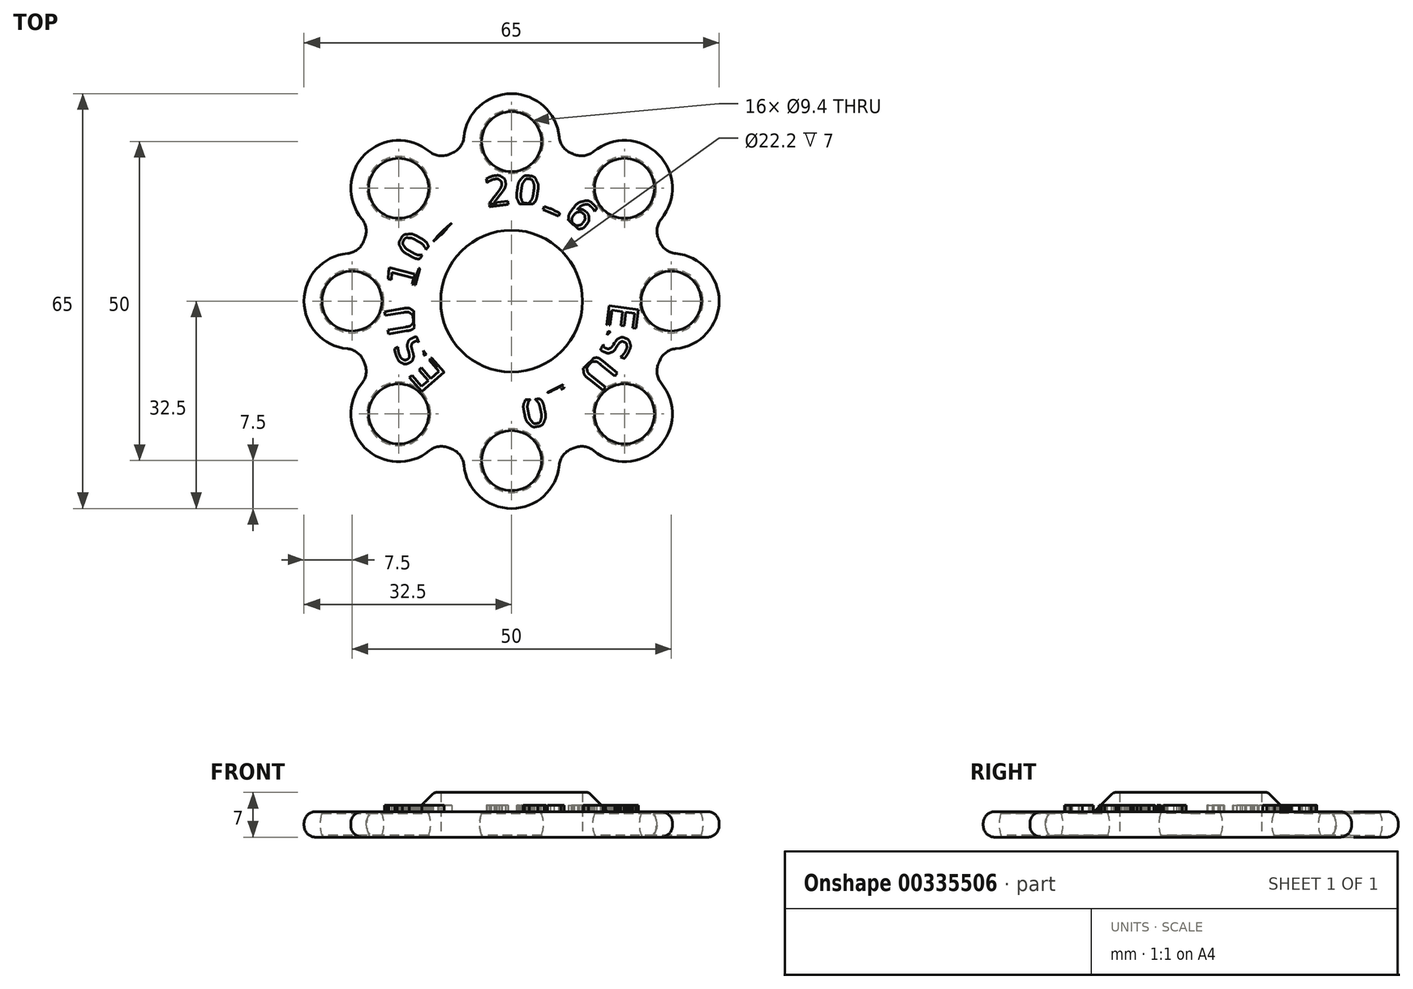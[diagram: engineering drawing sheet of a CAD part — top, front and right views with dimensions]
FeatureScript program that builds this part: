
annotation { "Feature Type Name" : "Feature", "Feature Type Description" : "" }
export const myFeature = defineFeature(function(context is Context, id is Id, definition is map)
    precondition{}
    {
        {
            var Q0;
            Q0=qCreatedBy(makeId("Top.planeOp"),FACE);
            var sketch = newSketch(context, id + "F0", { "sketchPlane" : qUnion([Q0])});
            skCircle(sketch, "E0", {"center": v(0, 0) * mm, "radius": 11.1 * mm});
            skPoint(sketch, "E1.0.midPoint", {"position": v(12.23, 6.82) * mm});
            skCircle(sketch, "E2", {"center": v(0, 25) * mm, "radius": 4.7 * mm});
            skCircle(sketch, "E3.1.0", {"center": v(-17.68, 17.68) * mm, "radius": 4.7 * mm});
            skCircle(sketch, "E3.2.0", {"center": v(-25, 0) * mm, "radius": 4.7 * mm});
            skCircle(sketch, "E3.3.0", {"center": v(-17.68, -17.68) * mm, "radius": 4.7 * mm});
            skCircle(sketch, "E3.4.0", {"center": v(0, -25) * mm, "radius": 4.7 * mm});
            skCircle(sketch, "E3.5.0", {"center": v(17.68, -17.68) * mm, "radius": 4.7 * mm});
            skCircle(sketch, "E3.6.0", {"center": v(25, 0) * mm, "radius": 4.7 * mm});
            skCircle(sketch, "E3.7.0", {"center": v(17.68, 17.68) * mm, "radius": 4.7 * mm});
            skCircle(sketch, "E4", {"center": v(0, 25) * mm, "radius": 7.5 * mm});
            skCircle(sketch, "E5.1.0", {"center": v(-17.68, 17.68) * mm, "radius": 7.5 * mm});
            skCircle(sketch, "E5.2.0", {"center": v(-25, 0) * mm, "radius": 7.5 * mm});
            skCircle(sketch, "E5.3.0", {"center": v(-17.68, -17.68) * mm, "radius": 7.5 * mm});
            skCircle(sketch, "E5.4.0", {"center": v(0, -25) * mm, "radius": 7.5 * mm});
            skCircle(sketch, "E5.5.0", {"center": v(17.68, -17.68) * mm, "radius": 7.5 * mm});
            skCircle(sketch, "E5.6.0", {"center": v(25, 0) * mm, "radius": 7.5 * mm});
            skCircle(sketch, "E5.7.0", {"center": v(17.68, 17.68) * mm, "radius": 7.5 * mm});
            skCircle(sketch, "E6", {"center": v(0, 0) * mm, "radius": 25 * mm});
            skSolve(sketch);
        }
        {
            var Q0;
            Q0=makeQuery(id+"F0.imprint","IMPRINT",FACE,{"disambiguationData":[TD([[makeQuery(id+"F0.imprint","IMPRINT",EDGE,{"derivedFrom":sQuery(id+"F0.wireOp",EDGE,"E0")}),-1.0]])]});
            var Q1;
            {var subQ0=sQuery(id+"F0.wireOp",EDGE,"E6");var subQ1=sQuery(id+"F0.wireOp",EDGE,"E3.3.0");var subQ2=makeQuery(id+"F0.imprint","INTERSECT",VERTEX,{"disambiguationData":[OD(0.0)],"derivedFrom":[subQ1,subQ0]});Q1=makeQuery(id+"F0.imprint","IMPRINT",FACE,{"disambiguationData":[TD([[makeQuery(id+"F0.imprint","IMPRINT",EDGE,{"disambiguationData":[TD([[subQ2,-1.0]])],"derivedFrom":subQ1}),-1.0]])]});}
            var Q2;
            {var subQ0=sQuery(id+"F0.wireOp",EDGE,"E6");var subQ1=sQuery(id+"F0.wireOp",EDGE,"E3.3.0");var subQ2=makeQuery(id+"F0.imprint","INTERSECT",VERTEX,{"disambiguationData":[OD(0.0)],"derivedFrom":[subQ1,subQ0]});Q2=makeQuery(id+"F0.imprint","IMPRINT",FACE,{"disambiguationData":[TD([[makeQuery(id+"F0.imprint","IMPRINT",EDGE,{"disambiguationData":[TD([[subQ2,1.0]])],"derivedFrom":subQ1}),-1.0]])]});}
            var Q3;
            {var subQ0=sQuery(id+"F0.wireOp",EDGE,"E6");var subQ1=sQuery(id+"F0.wireOp",EDGE,"E3.2.0");var subQ2=makeQuery(id+"F0.imprint","INTERSECT",VERTEX,{"disambiguationData":[OD(0.0)],"derivedFrom":[subQ1,subQ0]});Q3=makeQuery(id+"F0.imprint","IMPRINT",FACE,{"disambiguationData":[TD([[makeQuery(id+"F0.imprint","IMPRINT",EDGE,{"disambiguationData":[TD([[subQ2,1.0]])],"derivedFrom":subQ1}),-1.0]])]});}
            var Q4;
            {var subQ0=sQuery(id+"F0.wireOp",EDGE,"E6");var subQ1=sQuery(id+"F0.wireOp",EDGE,"E3.2.0");var subQ2=makeQuery(id+"F0.imprint","INTERSECT",VERTEX,{"disambiguationData":[OD(0.0)],"derivedFrom":[subQ1,subQ0]});Q4=makeQuery(id+"F0.imprint","IMPRINT",FACE,{"disambiguationData":[TD([[makeQuery(id+"F0.imprint","IMPRINT",EDGE,{"disambiguationData":[TD([[subQ2,-1.0]])],"derivedFrom":subQ1}),-1.0]])]});}
            var Q5;
            {var subQ0=sQuery(id+"F0.wireOp",EDGE,"E6");var subQ1=sQuery(id+"F0.wireOp",EDGE,"E3.1.0");var subQ2=makeQuery(id+"F0.imprint","INTERSECT",VERTEX,{"disambiguationData":[OD(0.0)],"derivedFrom":[subQ1,subQ0]});Q5=makeQuery(id+"F0.imprint","IMPRINT",FACE,{"disambiguationData":[TD([[makeQuery(id+"F0.imprint","IMPRINT",EDGE,{"disambiguationData":[TD([[subQ2,-1.0]])],"derivedFrom":subQ1}),-1.0]])]});}
            var Q6;
            {var subQ0=sQuery(id+"F0.wireOp",EDGE,"E6");var subQ1=sQuery(id+"F0.wireOp",EDGE,"E3.1.0");var subQ2=makeQuery(id+"F0.imprint","INTERSECT",VERTEX,{"disambiguationData":[OD(0.0)],"derivedFrom":[subQ1,subQ0]});Q6=makeQuery(id+"F0.imprint","IMPRINT",FACE,{"disambiguationData":[TD([[makeQuery(id+"F0.imprint","IMPRINT",EDGE,{"disambiguationData":[TD([[subQ2,1.0]])],"derivedFrom":subQ1}),-1.0]])]});}
            var Q7;
            {var subQ0=sQuery(id+"F0.wireOp",EDGE,"E6");var subQ1=sQuery(id+"F0.wireOp",EDGE,"E2");var subQ2=makeQuery(id+"F0.imprint","INTERSECT",VERTEX,{"disambiguationData":[OD(0.0)],"derivedFrom":[subQ1,subQ0]});Q7=makeQuery(id+"F0.imprint","IMPRINT",FACE,{"disambiguationData":[TD([[makeQuery(id+"F0.imprint","IMPRINT",EDGE,{"disambiguationData":[TD([[subQ2,1.0]])],"derivedFrom":subQ1}),-1.0]])]});}
            var Q8;
            {var subQ0=sQuery(id+"F0.wireOp",EDGE,"E6");var subQ1=sQuery(id+"F0.wireOp",EDGE,"E2");var subQ2=makeQuery(id+"F0.imprint","INTERSECT",VERTEX,{"disambiguationData":[OD(0.0)],"derivedFrom":[subQ1,subQ0]});Q8=makeQuery(id+"F0.imprint","IMPRINT",FACE,{"disambiguationData":[TD([[makeQuery(id+"F0.imprint","IMPRINT",EDGE,{"disambiguationData":[TD([[subQ2,-1.0]])],"derivedFrom":subQ1}),-1.0]])]});}
            var Q9;
            {var subQ0=sQuery(id+"F0.wireOp",EDGE,"E6");var subQ1=sQuery(id+"F0.wireOp",EDGE,"E3.7.0");var subQ2=makeQuery(id+"F0.imprint","INTERSECT",VERTEX,{"disambiguationData":[OD(0.0)],"derivedFrom":[subQ1,subQ0]});Q9=makeQuery(id+"F0.imprint","IMPRINT",FACE,{"disambiguationData":[TD([[makeQuery(id+"F0.imprint","IMPRINT",EDGE,{"disambiguationData":[TD([[subQ2,1.0]])],"derivedFrom":subQ1}),-1.0]])]});}
            var Q10;
            {var subQ0=sQuery(id+"F0.wireOp",EDGE,"E6");var subQ1=sQuery(id+"F0.wireOp",EDGE,"E3.7.0");var subQ2=makeQuery(id+"F0.imprint","INTERSECT",VERTEX,{"disambiguationData":[OD(0.0)],"derivedFrom":[subQ1,subQ0]});Q10=makeQuery(id+"F0.imprint","IMPRINT",FACE,{"disambiguationData":[TD([[makeQuery(id+"F0.imprint","IMPRINT",EDGE,{"disambiguationData":[TD([[subQ2,-1.0]])],"derivedFrom":subQ1}),-1.0]])]});}
            var Q11;
            {var subQ0=sQuery(id+"F0.wireOp",EDGE,"E6");var subQ1=sQuery(id+"F0.wireOp",EDGE,"E3.6.0");var subQ2=makeQuery(id+"F0.imprint","INTERSECT",VERTEX,{"disambiguationData":[OD(0.0)],"derivedFrom":[subQ1,subQ0]});Q11=makeQuery(id+"F0.imprint","IMPRINT",FACE,{"disambiguationData":[TD([[makeQuery(id+"F0.imprint","IMPRINT",EDGE,{"disambiguationData":[TD([[subQ2,-1.0]])],"derivedFrom":subQ1}),-1.0]])]});}
            var Q12;
            {var subQ0=sQuery(id+"F0.wireOp",EDGE,"E6");var subQ1=sQuery(id+"F0.wireOp",EDGE,"E3.6.0");var subQ2=makeQuery(id+"F0.imprint","INTERSECT",VERTEX,{"disambiguationData":[OD(0.0)],"derivedFrom":[subQ1,subQ0]});Q12=makeQuery(id+"F0.imprint","IMPRINT",FACE,{"disambiguationData":[TD([[makeQuery(id+"F0.imprint","IMPRINT",EDGE,{"disambiguationData":[TD([[subQ2,1.0]])],"derivedFrom":subQ1}),-1.0]])]});}
            var Q13;
            {var subQ0=sQuery(id+"F0.wireOp",EDGE,"E6");var subQ1=sQuery(id+"F0.wireOp",EDGE,"E3.5.0");var subQ2=makeQuery(id+"F0.imprint","INTERSECT",VERTEX,{"disambiguationData":[OD(0.0)],"derivedFrom":[subQ1,subQ0]});Q13=makeQuery(id+"F0.imprint","IMPRINT",FACE,{"disambiguationData":[TD([[makeQuery(id+"F0.imprint","IMPRINT",EDGE,{"disambiguationData":[TD([[subQ2,1.0]])],"derivedFrom":subQ1}),-1.0]])]});}
            var Q14;
            {var subQ0=sQuery(id+"F0.wireOp",EDGE,"E6");var subQ1=sQuery(id+"F0.wireOp",EDGE,"E3.5.0");var subQ2=makeQuery(id+"F0.imprint","INTERSECT",VERTEX,{"disambiguationData":[OD(0.0)],"derivedFrom":[subQ1,subQ0]});Q14=makeQuery(id+"F0.imprint","IMPRINT",FACE,{"disambiguationData":[TD([[makeQuery(id+"F0.imprint","IMPRINT",EDGE,{"disambiguationData":[TD([[subQ2,-1.0]])],"derivedFrom":subQ1}),-1.0]])]});}
            var Q15;
            {var subQ0=sQuery(id+"F0.wireOp",EDGE,"E6");var subQ1=sQuery(id+"F0.wireOp",EDGE,"E3.4.0");var subQ2=makeQuery(id+"F0.imprint","INTERSECT",VERTEX,{"disambiguationData":[OD(0.0)],"derivedFrom":[subQ1,subQ0]});Q15=makeQuery(id+"F0.imprint","IMPRINT",FACE,{"disambiguationData":[TD([[makeQuery(id+"F0.imprint","IMPRINT",EDGE,{"disambiguationData":[TD([[subQ2,1.0]])],"derivedFrom":subQ1}),-1.0]])]});}
            var Q16;
            {var subQ0=sQuery(id+"F0.wireOp",EDGE,"E6");var subQ1=sQuery(id+"F0.wireOp",EDGE,"E3.4.0");var subQ2=makeQuery(id+"F0.imprint","INTERSECT",VERTEX,{"disambiguationData":[OD(0.0)],"derivedFrom":[subQ1,subQ0]});Q16=makeQuery(id+"F0.imprint","IMPRINT",FACE,{"disambiguationData":[TD([[makeQuery(id+"F0.imprint","IMPRINT",EDGE,{"disambiguationData":[TD([[subQ2,-1.0]])],"derivedFrom":subQ1}),-1.0]])]});}
            extrude(context, id + "F1", {"entities" : qUnion([Q0, Q1, Q2, Q3, Q4, Q5, Q6, Q7, Q8, Q9, Q10, Q11, Q12, Q13, Q14, Q15, Q16]), "depth" : 2 * mm, "hasSecondDirection" : true, "secondDirectionOppositeDirection" : true, "secondDirectionDepth" : 2 * mm});
        }
        {
            var Q0;
            {var subQ0=sQuery(id+"F0.wireOp",EDGE,"E6");var subQ1=sQuery(id+"F0.wireOp",EDGE,"E5.4.0");Q0=makeQuery(id+"F1.opExtrude","SWEPT_EDGE",EDGE,{"disambiguationData":[OSD([subQ1,subQ0]),TDD([makeQuery(id+"F0.imprint","INTERSECT",VERTEX,{"disambiguationData":[OD(0.0)],"derivedFrom":[subQ1,subQ0]})])]});}
            var Q1;
            {var subQ0=sQuery(id+"F0.wireOp",EDGE,"E6");var subQ1=sQuery(id+"F0.wireOp",EDGE,"E5.2.0");Q1=makeQuery(id+"F1.opExtrude","SWEPT_EDGE",EDGE,{"disambiguationData":[OSD([subQ1,subQ0]),TDD([makeQuery(id+"F0.imprint","INTERSECT",VERTEX,{"disambiguationData":[OD(1.0)],"derivedFrom":[subQ1,subQ0]})])]});}
            var Q2;
            {var subQ0=sQuery(id+"F0.wireOp",EDGE,"E6");var subQ1=sQuery(id+"F0.wireOp",EDGE,"E5.2.0");Q2=makeQuery(id+"F1.opExtrude","SWEPT_EDGE",EDGE,{"disambiguationData":[OSD([subQ1,subQ0]),TDD([makeQuery(id+"F0.imprint","INTERSECT",VERTEX,{"disambiguationData":[OD(0.0)],"derivedFrom":[subQ1,subQ0]})])]});}
            var Q3;
            {var subQ0=sQuery(id+"F0.wireOp",EDGE,"E6");var subQ1=sQuery(id+"F0.wireOp",EDGE,"E4");Q3=makeQuery(id+"F1.opExtrude","SWEPT_EDGE",EDGE,{"disambiguationData":[OSD([subQ1,subQ0]),TDD([makeQuery(id+"F0.imprint","INTERSECT",VERTEX,{"disambiguationData":[OD(1.0)],"derivedFrom":[subQ1,subQ0]})])]});}
            var Q4;
            {var subQ0=sQuery(id+"F0.wireOp",EDGE,"E6");var subQ1=sQuery(id+"F0.wireOp",EDGE,"E5.7.0");Q4=makeQuery(id+"F1.opExtrude","SWEPT_EDGE",EDGE,{"disambiguationData":[OSD([subQ1,subQ0]),TDD([makeQuery(id+"F0.imprint","INTERSECT",VERTEX,{"disambiguationData":[OD(1.0)],"derivedFrom":[subQ1,subQ0]})])]});}
            var Q5;
            {var subQ0=sQuery(id+"F0.wireOp",EDGE,"E6");var subQ1=sQuery(id+"F0.wireOp",EDGE,"E5.1.0");Q5=makeQuery(id+"F1.opExtrude","SWEPT_EDGE",EDGE,{"disambiguationData":[OSD([subQ1,subQ0]),TDD([makeQuery(id+"F0.imprint","INTERSECT",VERTEX,{"disambiguationData":[OD(1.0)],"derivedFrom":[subQ1,subQ0]})])]});}
            var Q6;
            {var subQ0=sQuery(id+"F0.wireOp",EDGE,"E6");var subQ1=sQuery(id+"F0.wireOp",EDGE,"E5.3.0");Q6=makeQuery(id+"F1.opExtrude","SWEPT_EDGE",EDGE,{"disambiguationData":[OSD([subQ1,subQ0]),TDD([makeQuery(id+"F0.imprint","INTERSECT",VERTEX,{"disambiguationData":[OD(0.0)],"derivedFrom":[subQ1,subQ0]})])]});}
            var Q7;
            {var subQ0=sQuery(id+"F0.wireOp",EDGE,"E6");var subQ1=sQuery(id+"F0.wireOp",EDGE,"E5.1.0");Q7=makeQuery(id+"F1.opExtrude","SWEPT_EDGE",EDGE,{"disambiguationData":[OSD([subQ1,subQ0]),TDD([makeQuery(id+"F0.imprint","INTERSECT",VERTEX,{"disambiguationData":[OD(0.0)],"derivedFrom":[subQ1,subQ0]})])]});}
            var Q8;
            {var subQ0=sQuery(id+"F0.wireOp",EDGE,"E6");var subQ1=sQuery(id+"F0.wireOp",EDGE,"E4");Q8=makeQuery(id+"F1.opExtrude","SWEPT_EDGE",EDGE,{"disambiguationData":[OSD([subQ1,subQ0]),TDD([makeQuery(id+"F0.imprint","INTERSECT",VERTEX,{"disambiguationData":[OD(0.0)],"derivedFrom":[subQ1,subQ0]})])]});}
            var Q9;
            {var subQ0=sQuery(id+"F0.wireOp",EDGE,"E6");var subQ1=sQuery(id+"F0.wireOp",EDGE,"E5.6.0");Q9=makeQuery(id+"F1.opExtrude","SWEPT_EDGE",EDGE,{"disambiguationData":[OSD([subQ1,subQ0]),TDD([makeQuery(id+"F0.imprint","INTERSECT",VERTEX,{"disambiguationData":[OD(0.0)],"derivedFrom":[subQ1,subQ0]})])]});}
            var Q10;
            {var subQ0=sQuery(id+"F0.wireOp",EDGE,"E6");var subQ1=sQuery(id+"F0.wireOp",EDGE,"E5.7.0");Q10=makeQuery(id+"F1.opExtrude","SWEPT_EDGE",EDGE,{"disambiguationData":[OSD([subQ1,subQ0]),TDD([makeQuery(id+"F0.imprint","INTERSECT",VERTEX,{"disambiguationData":[OD(0.0)],"derivedFrom":[subQ1,subQ0]})])]});}
            var Q11;
            {var subQ0=sQuery(id+"F0.wireOp",EDGE,"E6");var subQ1=sQuery(id+"F0.wireOp",EDGE,"E5.6.0");Q11=makeQuery(id+"F1.opExtrude","SWEPT_EDGE",EDGE,{"disambiguationData":[OSD([subQ1,subQ0]),TDD([makeQuery(id+"F0.imprint","INTERSECT",VERTEX,{"disambiguationData":[OD(1.0)],"derivedFrom":[subQ1,subQ0]})])]});}
            var Q12;
            {var subQ0=sQuery(id+"F0.wireOp",EDGE,"E6");var subQ1=sQuery(id+"F0.wireOp",EDGE,"E5.5.0");Q12=makeQuery(id+"F1.opExtrude","SWEPT_EDGE",EDGE,{"disambiguationData":[OSD([subQ1,subQ0]),TDD([makeQuery(id+"F0.imprint","INTERSECT",VERTEX,{"disambiguationData":[OD(1.0)],"derivedFrom":[subQ1,subQ0]})])]});}
            var Q13;
            {var subQ0=sQuery(id+"F0.wireOp",EDGE,"E6");var subQ1=sQuery(id+"F0.wireOp",EDGE,"E5.5.0");Q13=makeQuery(id+"F1.opExtrude","SWEPT_EDGE",EDGE,{"disambiguationData":[OSD([subQ1,subQ0]),TDD([makeQuery(id+"F0.imprint","INTERSECT",VERTEX,{"disambiguationData":[OD(0.0)],"derivedFrom":[subQ1,subQ0]})])]});}
            var Q14;
            {var subQ0=sQuery(id+"F0.wireOp",EDGE,"E6");var subQ1=sQuery(id+"F0.wireOp",EDGE,"E5.4.0");Q14=makeQuery(id+"F1.opExtrude","SWEPT_EDGE",EDGE,{"disambiguationData":[OSD([subQ1,subQ0]),TDD([makeQuery(id+"F0.imprint","INTERSECT",VERTEX,{"disambiguationData":[OD(1.0)],"derivedFrom":[subQ1,subQ0]})])]});}
            var Q15;
            {var subQ0=sQuery(id+"F0.wireOp",EDGE,"E6");var subQ1=sQuery(id+"F0.wireOp",EDGE,"E5.3.0");Q15=makeQuery(id+"F1.opExtrude","SWEPT_EDGE",EDGE,{"disambiguationData":[OSD([subQ1,subQ0]),TDD([makeQuery(id+"F0.imprint","INTERSECT",VERTEX,{"disambiguationData":[OD(1.0)],"derivedFrom":[subQ1,subQ0]})])]});}
            fillet(context, id + "F2", {"entities" : qUnion([Q0, Q1, Q2, Q3, Q4, Q5, Q6, Q7, Q8, Q9, Q10, Q11, Q12, Q13, Q14, Q15]), "radius" : 3 * mm, "tangentPropagation" : true, "allowEdgeOverflow" : false});
        }
        {
            var Q0;
            Q0=makeQuery(id+"F1.opExtrude","CAP_EDGE",EDGE,{"disambiguationData":[OSD([sQuery(id+"F0.wireOp",EDGE,"E5.7.0")])],"isStart":false});
            var Q1;
            Q1=makeQuery(id+"F1.opExtrude","CAP_EDGE",EDGE,{"disambiguationData":[OSD([sQuery(id+"F0.wireOp",EDGE,"E5.7.0")])],"isStart":true});
            fillet(context, id + "F3", {"entities" : qUnion([Q0, Q1]), "radius" : 1.8 * mm, "tangentPropagation" : true, "allowEdgeOverflow" : false});
        }
        {
            var Q0;
            Q0=qCreatedBy(makeId("Right.planeOp"),FACE);
            var sketch = newSketch(context, id + "F4", { "sketchPlane" : qUnion([Q0])});
            skPoint(sketch, "E7.0", {"position": v(-25, 0) * mm});
            skPoint(sketch, "E7.1", {"position": v(25, 0) * mm});
            skLineSegment(sketch, "E8", {"start": v(-25, 12.35) * mm, "end": v(-25, -14.21) * mm, "construction": true});
            skLineSegment(sketch, "E9", {"start": v(25, 12.16) * mm, "end": v(25, -14.21) * mm, "construction": true});
            skPoint(sketch, "E10", {"position": v(-25, 5) * mm});
            skPoint(sketch, "E11", {"position": v(-25, -5) * mm});
            skPoint(sketch, "E12", {"position": v(25, 5) * mm});
            skPoint(sketch, "E13", {"position": v(25, -5) * mm});
            skArc(sketch, "E14", {"start": v(-25, 5) * mm, "mid": v(-30, 0) * mm, "end": v(-25, -5) * mm});
            skArc(sketch, "E15", {"start": v(25, -5) * mm, "mid": v(30, 0) * mm, "end": v(25, 5) * mm});
            skLineSegment(sketch, "E16", {"start": v(-25, 5) * mm, "end": v(-25, -5) * mm});
            skLineSegment(sketch, "E17", {"start": v(25, 5) * mm, "end": v(25, -5) * mm});
            skLineSegment(sketch, "E18", {"start": v(0, 41.23) * mm, "end": v(0, -49.38) * mm, "construction": true});
            skSolve(sketch);
        }
        {
            var Q0;
            Q0=makeQuery(id+"F4.imprint","IMPRINT",FACE,{"disambiguationData":[TD([[makeQuery(id+"F4.imprint","IMPRINT",EDGE,{"derivedFrom":sQuery(id+"F4.wireOp",EDGE,"E14")}),1.0]])]});
            var Q1;
            Q1=sQuery(id+"F4.wireOp",EDGE,"E8");
            revolve(context, id + "F5", {"entities" : qUnion([Q0]), "axis" : qUnion([Q1]), "revolveType" : RevolveType.FULL});
        }
        {
            var Q0;
            Q0=makeQuery(id+"F4.imprint","IMPRINT",FACE,{"disambiguationData":[TD([[makeQuery(id+"F4.imprint","IMPRINT",EDGE,{"derivedFrom":sQuery(id+"F4.wireOp",EDGE,"E15")}),1.0]])]});
            var Q1;
            Q1=sQuery(id+"F4.wireOp",EDGE,"E9");
            revolve(context, id + "F6", {"entities" : qUnion([Q0]), "axis" : qUnion([Q1]), "revolveType" : RevolveType.FULL});
        }
        {
            var Q0;
            Q0=makeQuery(id+"F6.opRevolve","SWEPT_BODY",BODY,{"disambiguationData":[OSD([sQuery(id+"F4.wireOp",EDGE,"E15"),sQuery(id+"F4.wireOp",EDGE,"E17")])]});
            var Q1;
            Q1=makeQuery(id+"F5.opRevolve","SWEPT_BODY",BODY,{"disambiguationData":[OSD([sQuery(id+"F4.wireOp",EDGE,"E14"),sQuery(id+"F4.wireOp",EDGE,"E16")])]});
            var Q2;
            Q2=makeQuery(id+"F1.opExtrude","SWEPT_BODY",BODY,{"disambiguationData":[OSD([sQuery(id+"F0.wireOp",EDGE,"E0"),sQuery(id+"F0.wireOp",EDGE,"E2"),sQuery(id+"F0.wireOp",EDGE,"E3.1.0"),sQuery(id+"F0.wireOp",EDGE,"E3.2.0"),sQuery(id+"F0.wireOp",EDGE,"E3.3.0"),sQuery(id+"F0.wireOp",EDGE,"E3.4.0"),sQuery(id+"F0.wireOp",EDGE,"E3.5.0"),sQuery(id+"F0.wireOp",EDGE,"E3.6.0"),sQuery(id+"F0.wireOp",EDGE,"E3.7.0"),sQuery(id+"F0.wireOp",EDGE,"E4"),sQuery(id+"F0.wireOp",EDGE,"E5.1.0"),sQuery(id+"F0.wireOp",EDGE,"E5.2.0"),sQuery(id+"F0.wireOp",EDGE,"E5.3.0"),sQuery(id+"F0.wireOp",EDGE,"E5.4.0"),sQuery(id+"F0.wireOp",EDGE,"E5.5.0"),sQuery(id+"F0.wireOp",EDGE,"E5.6.0"),sQuery(id+"F0.wireOp",EDGE,"E5.7.0"),sQuery(id+"F0.wireOp",EDGE,"E6")])]});
            booleanBodies(context, id + "F7", {"operationType" : BooleanOperationType.SUBTRACTION, "tools" : qUnion([Q0, Q1]), "targets" : qUnion([Q2])});
        }
        {
            var Q0;
            Q0=qCreatedBy(makeId("Front.planeOp"),FACE);
            var sketch = newSketch(context, id + "F8", { "sketchPlane" : qUnion([Q0])});
            skPoint(sketch, "E19.0", {"position": v(-25, 0) * mm});
            skPoint(sketch, "E19.1", {"position": v(25, 0) * mm});
            skLineSegment(sketch, "E20", {"start": v(-25, 18.9) * mm, "end": v(-25, -20.91) * mm, "construction": true});
            skLineSegment(sketch, "E21", {"start": v(25, 20.02) * mm, "end": v(25, -22.02) * mm, "construction": true});
            skPoint(sketch, "E22", {"position": v(-25, 5) * mm});
            skPoint(sketch, "E23", {"position": v(-25, -5) * mm});
            skPoint(sketch, "E24", {"position": v(25, 5) * mm});
            skPoint(sketch, "E25", {"position": v(25, -5) * mm});
            skArc(sketch, "E26", {"start": v(-25, 5) * mm, "mid": v(-30, 0) * mm, "end": v(-25, -5) * mm});
            skArc(sketch, "E27", {"start": v(25, -5) * mm, "mid": v(30, 0) * mm, "end": v(25, 5) * mm});
            skLineSegment(sketch, "E28", {"start": v(-25, 5) * mm, "end": v(-25, -5) * mm});
            skLineSegment(sketch, "E29", {"start": v(25, 5) * mm, "end": v(25, -5) * mm});
            skSolve(sketch);
        }
        {
            var Q0;
            Q0=makeQuery(id+"F8.imprint","IMPRINT",FACE,{"disambiguationData":[TD([[makeQuery(id+"F8.imprint","IMPRINT",EDGE,{"derivedFrom":sQuery(id+"F8.wireOp",EDGE,"E26")}),1.0]])]});
            var Q1;
            Q1=sQuery(id+"F8.wireOp",EDGE,"E20");
            revolve(context, id + "F9", {"entities" : qUnion([Q0]), "axis" : qUnion([Q1]), "revolveType" : RevolveType.FULL});
        }
        {
            var Q0;
            Q0=makeQuery(id+"F8.imprint","IMPRINT",FACE,{"disambiguationData":[TD([[makeQuery(id+"F8.imprint","IMPRINT",EDGE,{"derivedFrom":sQuery(id+"F8.wireOp",EDGE,"E27")}),1.0]])]});
            var Q1;
            Q1=sQuery(id+"F8.wireOp",EDGE,"E21");
            revolve(context, id + "F10", {"entities" : qUnion([Q0]), "axis" : qUnion([Q1]), "revolveType" : RevolveType.FULL});
        }
        {
            var Q0;
            Q0=makeQuery(id+"F9.opRevolve","SWEPT_BODY",BODY,{"disambiguationData":[OSD([sQuery(id+"F8.wireOp",EDGE,"E26"),sQuery(id+"F8.wireOp",EDGE,"E28")])]});
            var Q1;
            Q1=makeQuery(id+"F10.opRevolve","SWEPT_BODY",BODY,{"disambiguationData":[OSD([sQuery(id+"F8.wireOp",EDGE,"E27"),sQuery(id+"F8.wireOp",EDGE,"E29")])]});
            var Q2;
            Q2=makeQuery(id+"F1.opExtrude","SWEPT_BODY",BODY,{"disambiguationData":[OSD([sQuery(id+"F0.wireOp",EDGE,"E0"),sQuery(id+"F0.wireOp",EDGE,"E2"),sQuery(id+"F0.wireOp",EDGE,"E3.1.0"),sQuery(id+"F0.wireOp",EDGE,"E3.2.0"),sQuery(id+"F0.wireOp",EDGE,"E3.3.0"),sQuery(id+"F0.wireOp",EDGE,"E3.4.0"),sQuery(id+"F0.wireOp",EDGE,"E3.5.0"),sQuery(id+"F0.wireOp",EDGE,"E3.6.0"),sQuery(id+"F0.wireOp",EDGE,"E3.7.0"),sQuery(id+"F0.wireOp",EDGE,"E4"),sQuery(id+"F0.wireOp",EDGE,"E5.1.0"),sQuery(id+"F0.wireOp",EDGE,"E5.2.0"),sQuery(id+"F0.wireOp",EDGE,"E5.3.0"),sQuery(id+"F0.wireOp",EDGE,"E5.4.0"),sQuery(id+"F0.wireOp",EDGE,"E5.5.0"),sQuery(id+"F0.wireOp",EDGE,"E5.6.0"),sQuery(id+"F0.wireOp",EDGE,"E5.7.0"),sQuery(id+"F0.wireOp",EDGE,"E6")])]});
            booleanBodies(context, id + "F11", {"operationType" : BooleanOperationType.SUBTRACTION, "tools" : qUnion([Q0, Q1]), "targets" : qUnion([Q2])});
        }
        {
            var Q0;
            Q0=qCreatedBy(makeId("Front.planeOp"),FACE);
            var Q1;
            Q1=sQuery(id+"F0.wireOp",VERTEX,"E3.3.0.center");
            cPlane(context, id + "F12", {"entities" : qUnion([Q0, Q1]), "cplaneType" : CPlaneType.PLANE_POINT, "offset" : 25 * mm, "width" : 150 * mm, "height" : 150 * mm});
        }
        {
            var Q0;
            Q0=qCreatedBy(id+"F12.planeOp",FACE);
            var sketch = newSketch(context, id + "F13", { "sketchPlane" : qUnion([Q0])});
            skPoint(sketch, "E30.0", {"position": v(-17.68, 0) * mm});
            skPoint(sketch, "E30.1", {"position": v(17.68, 0) * mm});
            skLineSegment(sketch, "E31", {"start": v(-17.68, 20.76) * mm, "end": v(-17.68, -25.8) * mm, "construction": true});
            skLineSegment(sketch, "E32", {"start": v(17.68, 18.25) * mm, "end": v(17.68, -22.97) * mm, "construction": true});
            skPoint(sketch, "E33", {"position": v(-17.68, 5) * mm});
            skPoint(sketch, "E34", {"position": v(-17.68, -5) * mm});
            skPoint(sketch, "E35", {"position": v(17.68, -5) * mm});
            skPoint(sketch, "E36", {"position": v(17.68, 5) * mm});
            skArc(sketch, "E37", {"start": v(-17.68, 5) * mm, "mid": v(-22.68, 0) * mm, "end": v(-17.68, -5) * mm});
            skArc(sketch, "E38", {"start": v(17.68, -5) * mm, "mid": v(22.68, 0) * mm, "end": v(17.68, 5) * mm});
            skLineSegment(sketch, "E39", {"start": v(-17.68, 5) * mm, "end": v(-17.68, -5) * mm});
            skLineSegment(sketch, "E40", {"start": v(17.68, 5) * mm, "end": v(17.68, -5) * mm});
            skSolve(sketch);
        }
        {
            var Q0;
            Q0=makeQuery(id+"F13.imprint","IMPRINT",FACE,{"disambiguationData":[TD([[makeQuery(id+"F13.imprint","IMPRINT",EDGE,{"derivedFrom":sQuery(id+"F13.wireOp",EDGE,"E37")}),1.0]])]});
            var Q1;
            Q1=sQuery(id+"F13.wireOp",EDGE,"E31");
            revolve(context, id + "F14", {"entities" : qUnion([Q0]), "axis" : qUnion([Q1]), "revolveType" : RevolveType.FULL});
        }
        {
            var Q0;
            Q0=makeQuery(id+"F13.imprint","IMPRINT",FACE,{"disambiguationData":[TD([[makeQuery(id+"F13.imprint","IMPRINT",EDGE,{"derivedFrom":sQuery(id+"F13.wireOp",EDGE,"E38")}),1.0]])]});
            var Q1;
            Q1=sQuery(id+"F13.wireOp",EDGE,"E32");
            revolve(context, id + "F15", {"entities" : qUnion([Q0]), "axis" : qUnion([Q1]), "revolveType" : RevolveType.FULL});
        }
        {
            var Q0;
            Q0=makeQuery(id+"F15.opRevolve","SWEPT_BODY",BODY,{"disambiguationData":[OSD([sQuery(id+"F13.wireOp",EDGE,"E38"),sQuery(id+"F13.wireOp",EDGE,"E40")])]});
            var Q1;
            Q1=makeQuery(id+"F14.opRevolve","SWEPT_BODY",BODY,{"disambiguationData":[OSD([sQuery(id+"F13.wireOp",EDGE,"E37"),sQuery(id+"F13.wireOp",EDGE,"E39")])]});
            var Q2;
            Q2=makeQuery(id+"F1.opExtrude","SWEPT_BODY",BODY,{"disambiguationData":[OSD([sQuery(id+"F0.wireOp",EDGE,"E0"),sQuery(id+"F0.wireOp",EDGE,"E2"),sQuery(id+"F0.wireOp",EDGE,"E3.1.0"),sQuery(id+"F0.wireOp",EDGE,"E3.2.0"),sQuery(id+"F0.wireOp",EDGE,"E3.3.0"),sQuery(id+"F0.wireOp",EDGE,"E3.4.0"),sQuery(id+"F0.wireOp",EDGE,"E3.5.0"),sQuery(id+"F0.wireOp",EDGE,"E3.6.0"),sQuery(id+"F0.wireOp",EDGE,"E3.7.0"),sQuery(id+"F0.wireOp",EDGE,"E4"),sQuery(id+"F0.wireOp",EDGE,"E5.1.0"),sQuery(id+"F0.wireOp",EDGE,"E5.2.0"),sQuery(id+"F0.wireOp",EDGE,"E5.3.0"),sQuery(id+"F0.wireOp",EDGE,"E5.4.0"),sQuery(id+"F0.wireOp",EDGE,"E5.5.0"),sQuery(id+"F0.wireOp",EDGE,"E5.6.0"),sQuery(id+"F0.wireOp",EDGE,"E5.7.0"),sQuery(id+"F0.wireOp",EDGE,"E6")])]});
            booleanBodies(context, id + "F16", {"operationType" : BooleanOperationType.SUBTRACTION, "tools" : qUnion([Q0, Q1]), "targets" : qUnion([Q2])});
        }
        {
            var Q0;
            Q0=qCreatedBy(makeId("Front.planeOp"),FACE);
            var Q1;
            Q1=sQuery(id+"F0.wireOp",VERTEX,"E5.7.0.center");
            cPlane(context, id + "F17", {"entities" : qUnion([Q0, Q1]), "cplaneType" : CPlaneType.PLANE_POINT, "offset" : 25 * mm, "width" : 150 * mm, "height" : 150 * mm});
        }
        {
            var Q0;
            Q0=qCreatedBy(id+"F17.planeOp",FACE);
            var sketch = newSketch(context, id + "F18", { "sketchPlane" : qUnion([Q0])});
            skPoint(sketch, "E41.0", {"position": v(17.68, 0) * mm});
            skPoint(sketch, "E41.1", {"position": v(-17.68, 0) * mm});
            skLineSegment(sketch, "E42", {"start": v(17.68, 20.69) * mm, "end": v(17.68, -19.13) * mm, "construction": true});
            skLineSegment(sketch, "E43", {"start": v(-17.68, 22.25) * mm, "end": v(-17.68, -19.13) * mm, "construction": true});
            skPoint(sketch, "E44", {"position": v(17.68, 5) * mm});
            skPoint(sketch, "E45", {"position": v(-17.68, 5) * mm});
            skPoint(sketch, "E46", {"position": v(17.68, -5) * mm});
            skPoint(sketch, "E47", {"position": v(-17.68, -5) * mm});
            skArc(sketch, "E48", {"start": v(17.68, -5) * mm, "mid": v(22.68, 0) * mm, "end": v(17.68, 5) * mm});
            skArc(sketch, "E49", {"start": v(-17.68, 5) * mm, "mid": v(-22.68, 0) * mm, "end": v(-17.68, -5) * mm});
            skLineSegment(sketch, "E50", {"start": v(17.68, 5) * mm, "end": v(17.68, -5) * mm});
            skLineSegment(sketch, "E51", {"start": v(-17.68, 5) * mm, "end": v(-17.68, -5) * mm});
            skSolve(sketch);
        }
        {
            var Q0;
            Q0=makeQuery(id+"F18.imprint","IMPRINT",FACE,{"disambiguationData":[TD([[makeQuery(id+"F18.imprint","IMPRINT",EDGE,{"derivedFrom":sQuery(id+"F18.wireOp",EDGE,"E48")}),1.0]])]});
            var Q1;
            Q1=sQuery(id+"F18.wireOp",EDGE,"E42");
            revolve(context, id + "F19", {"entities" : qUnion([Q0]), "axis" : qUnion([Q1]), "revolveType" : RevolveType.FULL});
        }
        {
            var Q0;
            Q0=makeQuery(id+"F18.imprint","IMPRINT",FACE,{"disambiguationData":[TD([[makeQuery(id+"F18.imprint","IMPRINT",EDGE,{"derivedFrom":sQuery(id+"F18.wireOp",EDGE,"E49")}),1.0]])]});
            var Q1;
            Q1=sQuery(id+"F18.wireOp",EDGE,"E43");
            revolve(context, id + "F20", {"entities" : qUnion([Q0]), "axis" : qUnion([Q1]), "revolveType" : RevolveType.FULL});
        }
        {
            var Q0;
            Q0=makeQuery(id+"F20.opRevolve","SWEPT_BODY",BODY,{"disambiguationData":[OSD([sQuery(id+"F18.wireOp",EDGE,"E49"),sQuery(id+"F18.wireOp",EDGE,"E51")])]});
            var Q1;
            Q1=makeQuery(id+"F19.opRevolve","SWEPT_BODY",BODY,{"disambiguationData":[OSD([sQuery(id+"F18.wireOp",EDGE,"E48"),sQuery(id+"F18.wireOp",EDGE,"E50")])]});
            var Q2;
            Q2=makeQuery(id+"F1.opExtrude","SWEPT_BODY",BODY,{"disambiguationData":[OSD([sQuery(id+"F0.wireOp",EDGE,"E0"),sQuery(id+"F0.wireOp",EDGE,"E2"),sQuery(id+"F0.wireOp",EDGE,"E3.1.0"),sQuery(id+"F0.wireOp",EDGE,"E3.2.0"),sQuery(id+"F0.wireOp",EDGE,"E3.3.0"),sQuery(id+"F0.wireOp",EDGE,"E3.4.0"),sQuery(id+"F0.wireOp",EDGE,"E3.5.0"),sQuery(id+"F0.wireOp",EDGE,"E3.6.0"),sQuery(id+"F0.wireOp",EDGE,"E3.7.0"),sQuery(id+"F0.wireOp",EDGE,"E4"),sQuery(id+"F0.wireOp",EDGE,"E5.1.0"),sQuery(id+"F0.wireOp",EDGE,"E5.2.0"),sQuery(id+"F0.wireOp",EDGE,"E5.3.0"),sQuery(id+"F0.wireOp",EDGE,"E5.4.0"),sQuery(id+"F0.wireOp",EDGE,"E5.5.0"),sQuery(id+"F0.wireOp",EDGE,"E5.6.0"),sQuery(id+"F0.wireOp",EDGE,"E5.7.0"),sQuery(id+"F0.wireOp",EDGE,"E6")])]});
            booleanBodies(context, id + "F21", {"operationType" : BooleanOperationType.SUBTRACTION, "tools" : qUnion([Q0, Q1]), "targets" : qUnion([Q2])});
        }
        {
            var Q0;
            Q0=makeQuery(id+"F1.opExtrude","CAP_FACE",FACE,{"disambiguationData":[OSD([sQuery(id+"F0.wireOp",EDGE,"E0"),sQuery(id+"F0.wireOp",EDGE,"E2"),sQuery(id+"F0.wireOp",EDGE,"E3.1.0"),sQuery(id+"F0.wireOp",EDGE,"E3.2.0"),sQuery(id+"F0.wireOp",EDGE,"E3.3.0"),sQuery(id+"F0.wireOp",EDGE,"E3.4.0"),sQuery(id+"F0.wireOp",EDGE,"E3.5.0"),sQuery(id+"F0.wireOp",EDGE,"E3.6.0"),sQuery(id+"F0.wireOp",EDGE,"E3.7.0"),sQuery(id+"F0.wireOp",EDGE,"E4"),sQuery(id+"F0.wireOp",EDGE,"E5.1.0"),sQuery(id+"F0.wireOp",EDGE,"E5.2.0"),sQuery(id+"F0.wireOp",EDGE,"E5.3.0"),sQuery(id+"F0.wireOp",EDGE,"E5.4.0"),sQuery(id+"F0.wireOp",EDGE,"E5.5.0"),sQuery(id+"F0.wireOp",EDGE,"E5.6.0"),sQuery(id+"F0.wireOp",EDGE,"E5.7.0"),sQuery(id+"F0.wireOp",EDGE,"E6")])],"isStart":false});
            var sketch = newSketch(context, id + "F22", { "sketchPlane" : qUnion([Q0])});
            skCircle(sketch, "E52.0", {"center": v(0, 0) * mm, "radius": 11.1 * mm});
            skCircle(sketch, "E53.0", {"center": v(0, 0) * mm, "radius": 15.1 * mm});
            skSolve(sketch);
        }
        {
            var Q0;
            Q0=makeQuery(id+"F22.imprint","IMPRINT",FACE,{"disambiguationData":[TD([[makeQuery(id+"F22.imprint","IMPRINT",EDGE,{"derivedFrom":sQuery(id+"F22.wireOp",EDGE,"E52.0")}),-1.0]])]});
            extrude(context, id + "F23", {"entities" : qUnion([Q0]), "operationType" : NewBodyOperationType.ADD, "depth" : 3 * mm});
        }
        {
            var Q0;
            Q0=makeQuery(id+"F23.opExtrude","CAP_EDGE",EDGE,{"disambiguationData":[OSD([sQuery(id+"F22.wireOp",EDGE,"E53.0")])],"isStart":false});
            chamfer(context, id + "F24", {"entities" : qUnion([Q0]), "width" : 3 * mm, "tangentPropagation" : true});
        }
        {
            var Q0;
            Q0=makeQuery(id+"F24.opChamfer","BLEND_EDGE",EDGE,{"blendedFrom":[makeQuery(id+"F23.opExtrude","CAP_EDGE",EDGE,{"disambiguationData":[OSD([sQuery(id+"F22.wireOp",EDGE,"E53.0")])],"isStart":false}),makeQuery(id+"F1.opExtrude","CAP_FACE",FACE,{"disambiguationData":[OSD([sQuery(id+"F0.wireOp",EDGE,"E0"),sQuery(id+"F0.wireOp",EDGE,"E2"),sQuery(id+"F0.wireOp",EDGE,"E3.1.0"),sQuery(id+"F0.wireOp",EDGE,"E3.2.0"),sQuery(id+"F0.wireOp",EDGE,"E3.3.0"),sQuery(id+"F0.wireOp",EDGE,"E3.4.0"),sQuery(id+"F0.wireOp",EDGE,"E3.5.0"),sQuery(id+"F0.wireOp",EDGE,"E3.6.0"),sQuery(id+"F0.wireOp",EDGE,"E3.7.0"),sQuery(id+"F0.wireOp",EDGE,"E4"),sQuery(id+"F0.wireOp",EDGE,"E5.1.0"),sQuery(id+"F0.wireOp",EDGE,"E5.2.0"),sQuery(id+"F0.wireOp",EDGE,"E5.3.0"),sQuery(id+"F0.wireOp",EDGE,"E5.4.0"),sQuery(id+"F0.wireOp",EDGE,"E5.5.0"),sQuery(id+"F0.wireOp",EDGE,"E5.6.0"),sQuery(id+"F0.wireOp",EDGE,"E5.7.0"),sQuery(id+"F0.wireOp",EDGE,"E6")])],"isStart":false})],"blendedInto":[makeQuery(id+"F1.opExtrude","CAP_FACE",FACE,{"disambiguationData":[OSD([sQuery(id+"F0.wireOp",EDGE,"E0"),sQuery(id+"F0.wireOp",EDGE,"E2"),sQuery(id+"F0.wireOp",EDGE,"E3.1.0"),sQuery(id+"F0.wireOp",EDGE,"E3.2.0"),sQuery(id+"F0.wireOp",EDGE,"E3.3.0"),sQuery(id+"F0.wireOp",EDGE,"E3.4.0"),sQuery(id+"F0.wireOp",EDGE,"E3.5.0"),sQuery(id+"F0.wireOp",EDGE,"E3.6.0"),sQuery(id+"F0.wireOp",EDGE,"E3.7.0"),sQuery(id+"F0.wireOp",EDGE,"E4"),sQuery(id+"F0.wireOp",EDGE,"E5.1.0"),sQuery(id+"F0.wireOp",EDGE,"E5.2.0"),sQuery(id+"F0.wireOp",EDGE,"E5.3.0"),sQuery(id+"F0.wireOp",EDGE,"E5.4.0"),sQuery(id+"F0.wireOp",EDGE,"E5.5.0"),sQuery(id+"F0.wireOp",EDGE,"E5.6.0"),sQuery(id+"F0.wireOp",EDGE,"E5.7.0"),sQuery(id+"F0.wireOp",EDGE,"E6")])],"isStart":false})]});
            var Q1;
            {var subQ0=sQuery(id+"F22.wireOp",EDGE,"E53.0");Q1=makeQuery(id+"F24.opChamfer","BLEND_EDGE",EDGE,{"blendedFrom":[makeQuery(id+"F23.opExtrude","CAP_EDGE",EDGE,{"disambiguationData":[OSD([subQ0])],"isStart":false}),makeQuery(id+"F23.opExtrude","CAP_FACE",FACE,{"disambiguationData":[OSD([sQuery(id+"F22.wireOp",EDGE,"E52.0"),subQ0])],"isStart":false})],"blendedInto":[makeQuery(id+"F23.opExtrude","CAP_FACE",FACE,{"disambiguationData":[OSD([sQuery(id+"F22.wireOp",EDGE,"E52.0"),subQ0])],"isStart":false})]});}
            fillet(context, id + "F25", {"entities" : qUnion([Q0, Q1]), "radius" : .75 * mm, "tangentPropagation" : true, "allowEdgeOverflow" : false});
        }
        {
            var Q0;
            Q0=makeQuery(id+"F1.opExtrude","CAP_FACE",FACE,{"disambiguationData":[OSD([sQuery(id+"F0.wireOp",EDGE,"E0"),sQuery(id+"F0.wireOp",EDGE,"E2"),sQuery(id+"F0.wireOp",EDGE,"E3.1.0"),sQuery(id+"F0.wireOp",EDGE,"E3.2.0"),sQuery(id+"F0.wireOp",EDGE,"E3.3.0"),sQuery(id+"F0.wireOp",EDGE,"E3.4.0"),sQuery(id+"F0.wireOp",EDGE,"E3.5.0"),sQuery(id+"F0.wireOp",EDGE,"E3.6.0"),sQuery(id+"F0.wireOp",EDGE,"E3.7.0"),sQuery(id+"F0.wireOp",EDGE,"E4"),sQuery(id+"F0.wireOp",EDGE,"E5.1.0"),sQuery(id+"F0.wireOp",EDGE,"E5.2.0"),sQuery(id+"F0.wireOp",EDGE,"E5.3.0"),sQuery(id+"F0.wireOp",EDGE,"E5.4.0"),sQuery(id+"F0.wireOp",EDGE,"E5.5.0"),sQuery(id+"F0.wireOp",EDGE,"E5.6.0"),sQuery(id+"F0.wireOp",EDGE,"E5.7.0"),sQuery(id+"F0.wireOp",EDGE,"E6")])],"isStart":false});
            var sketch = newSketch(context, id + "F26", { "sketchPlane" : qUnion([Q0])});
            skFitSpline(sketch, "E54", {"points": [v(15.23, -0.11) * mm, v(15.23, -4.15) * mm, v(13.63, -8.02) * mm, v(10.77, -10.88) * mm]});
            skFitSpline(sketch, "E55", {"points": [v(10.77, -10.88) * mm, v(7.92, -13.73) * mm, v(4.04, -15.34) * mm, v(0, -15.34) * mm]});
            skFitSpline(sketch, "E56", {"points": [v(0, -15.34) * mm, v(-4.03, -15.34) * mm, v(-7.9, -13.73) * mm, v(-10.76, -10.88) * mm]});
            skFitSpline(sketch, "E57", {"points": [v(-10.76, -10.88) * mm, v(-13.62, -8.02) * mm, v(-15.22, -4.15) * mm, v(-15.22, -0.11) * mm]});
            skFitSpline(sketch, "E58", {"points": [v(-15.22, -0.11) * mm, v(-15.22, 3.93) * mm, v(-13.62, 7.8) * mm, v(-10.76, 10.65) * mm]});
            skFitSpline(sketch, "E59", {"points": [v(-10.76, 10.65) * mm, v(-7.9, 13.5) * mm, v(-4.03, 15.11) * mm, v(0, 15.11) * mm]});
            skFitSpline(sketch, "E60", {"points": [v(0, 15.11) * mm, v(4.04, 15.11) * mm, v(7.92, 13.5) * mm, v(10.77, 10.65) * mm]});
            skFitSpline(sketch, "E61", {"points": [v(10.77, 10.65) * mm, v(13.63, 7.8) * mm, v(15.23, 3.93) * mm, v(15.23, -0.11) * mm]});
            skLineSegment(sketch, "E62", {"start": v(19.87, -1.34) * mm, "end": v(19.49, -4.25) * mm});
            skLineSegment(sketch, "E63", {"start": v(19.49, -4.25) * mm, "end": v(18.97, -4.18) * mm});
            skLineSegment(sketch, "E64", {"start": v(18.97, -4.18) * mm, "end": v(19.27, -1.9) * mm});
            skLineSegment(sketch, "E65", {"start": v(19.27, -1.9) * mm, "end": v(17.9, -1.72) * mm});
            skLineSegment(sketch, "E66", {"start": v(17.9, -1.72) * mm, "end": v(17.62, -3.9) * mm});
            skLineSegment(sketch, "E67", {"start": v(17.62, -3.9) * mm, "end": v(17.1, -3.83) * mm});
            skLineSegment(sketch, "E68", {"start": v(17.1, -3.83) * mm, "end": v(17.38, -1.65) * mm});
            skLineSegment(sketch, "E69", {"start": v(17.38, -1.65) * mm, "end": v(15.72, -1.43) * mm});
            skLineSegment(sketch, "E70", {"start": v(15.72, -1.43) * mm, "end": v(15.41, -3.77) * mm});
            skLineSegment(sketch, "E71", {"start": v(15.41, -3.77) * mm, "end": v(14.9, -3.7) * mm});
            skLineSegment(sketch, "E72", {"start": v(14.9, -3.7) * mm, "end": v(15.28, -0.74) * mm});
            skLineSegment(sketch, "E73", {"start": v(15.28, -0.74) * mm, "end": v(19.87, -1.34) * mm});
            skLineSegment(sketch, "E74", {"start": v(17.66, -8.98) * mm, "end": v(17.1, -8.75) * mm});
            skFitSpline(sketch, "E75", {"points": [v(17.1, -8.75) * mm, v(17.29, -8.57) * mm, v(17.45, -8.4) * mm, v(17.59, -8.22) * mm]});
            skFitSpline(sketch, "E76", {"points": [v(17.59, -8.22) * mm, v(17.72, -8.05) * mm, v(17.82, -7.87) * mm, v(17.9, -7.7) * mm]});
            skFitSpline(sketch, "E77", {"points": [v(17.9, -7.7) * mm, v(18.03, -7.38) * mm, v(18.07, -7.1) * mm, v(18.02, -6.89) * mm]});
            skFitSpline(sketch, "E78", {"points": [v(18.02, -6.89) * mm, v(17.97, -6.67) * mm, v(17.83, -6.5) * mm, v(17.6, -6.41) * mm]});
            skFitSpline(sketch, "E79", {"points": [v(17.6, -6.41) * mm, v(17.42, -6.33) * mm, v(17.25, -6.33) * mm, v(17.1, -6.4) * mm]});
            skFitSpline(sketch, "E80", {"points": [v(17.1, -6.4) * mm, v(16.96, -6.48) * mm, v(16.8, -6.66) * mm, v(16.6, -6.95) * mm]});
            skLineSegment(sketch, "E81", {"start": v(16.6, -6.95) * mm, "end": v(16.39, -7.27) * mm});
            skFitSpline(sketch, "E82", {"points": [v(16.39, -7.27) * mm, v(16.13, -7.67) * mm, v(15.85, -7.93) * mm, v(15.56, -8.04) * mm]});
            skFitSpline(sketch, "E83", {"points": [v(15.56, -8.04) * mm, v(15.26, -8.16) * mm, v(14.94, -8.15) * mm, v(14.6, -8) * mm]});
            skFitSpline(sketch, "E84", {"points": [v(14.6, -8) * mm, v(14.18, -7.83) * mm, v(13.93, -7.56) * mm, v(13.83, -7.2) * mm]});
            skFitSpline(sketch, "E85", {"points": [v(13.83, -7.2) * mm, v(13.73, -6.83) * mm, v(13.8, -6.38) * mm, v(14.02, -5.84) * mm]});
            skFitSpline(sketch, "E86", {"points": [v(14.02, -5.84) * mm, v(14.1, -5.64) * mm, v(14.22, -5.43) * mm, v(14.36, -5.22) * mm]});
            skFitSpline(sketch, "E87", {"points": [v(14.36, -5.22) * mm, v(14.5, -5.01) * mm, v(14.67, -4.8) * mm, v(14.86, -4.6) * mm]});
            skLineSegment(sketch, "E88", {"start": v(14.86, -4.6) * mm, "end": v(15.45, -4.85) * mm});
            skFitSpline(sketch, "E89", {"points": [v(15.45, -4.85) * mm, v(15.22, -5.03) * mm, v(15.03, -5.22) * mm, v(14.87, -5.41) * mm]});
            skFitSpline(sketch, "E90", {"points": [v(14.87, -5.41) * mm, v(14.7, -5.61) * mm, v(14.58, -5.82) * mm, v(14.49, -6.04) * mm]});
            skFitSpline(sketch, "E91", {"points": [v(14.49, -6.04) * mm, v(14.35, -6.37) * mm, v(14.3, -6.65) * mm, v(14.36, -6.88) * mm]});
            skFitSpline(sketch, "E92", {"points": [v(14.36, -6.88) * mm, v(14.42, -7.12) * mm, v(14.57, -7.28) * mm, v(14.8, -7.38) * mm]});
            skFitSpline(sketch, "E93", {"points": [v(14.8, -7.38) * mm, v(15.02, -7.47) * mm, v(15.2, -7.47) * mm, v(15.38, -7.4) * mm]});
            skFitSpline(sketch, "E94", {"points": [v(15.38, -7.4) * mm, v(15.55, -7.32) * mm, v(15.73, -7.14) * mm, v(15.9, -6.87) * mm]});
            skLineSegment(sketch, "E95", {"start": v(15.9, -6.87) * mm, "end": v(16.13, -6.55) * mm});
            skFitSpline(sketch, "E96", {"points": [v(16.13, -6.55) * mm, v(16.4, -6.15) * mm, v(16.66, -5.9) * mm, v(16.92, -5.78) * mm]});
            skFitSpline(sketch, "E97", {"points": [v(16.92, -5.78) * mm, v(17.18, -5.67) * mm, v(17.48, -5.68) * mm, v(17.8, -5.81) * mm]});
            skFitSpline(sketch, "E98", {"points": [v(17.8, -5.81) * mm, v(18.18, -5.97) * mm, v(18.42, -6.23) * mm, v(18.53, -6.58) * mm]});
            skFitSpline(sketch, "E99", {"points": [v(18.53, -6.58) * mm, v(18.64, -6.94) * mm, v(18.6, -7.36) * mm, v(18.4, -7.82) * mm]});
            skFitSpline(sketch, "E100", {"points": [v(18.4, -7.82) * mm, v(18.31, -8.02) * mm, v(18.2, -8.22) * mm, v(18.09, -8.41) * mm]});
            skFitSpline(sketch, "E101", {"points": [v(18.09, -8.41) * mm, v(17.96, -8.6) * mm, v(17.82, -8.8) * mm, v(17.66, -8.98) * mm]});
            skLineSegment(sketch, "E102", {"start": v(17.66, -8.98) * mm, "end": v(17.66, -8.98) * mm});
            skLineSegment(sketch, "E103", {"start": v(16.54, -11.24) * mm, "end": v(16.15, -11.73) * mm});
            skLineSegment(sketch, "E104", {"start": v(16.15, -11.73) * mm, "end": v(13.96, -9.96) * mm});
            skFitSpline(sketch, "E105", {"points": [v(13.96, -9.96) * mm, v(13.58, -9.65) * mm, v(13.24, -9.49) * mm, v(12.96, -9.5) * mm]});
            skFitSpline(sketch, "E106", {"points": [v(12.96, -9.5) * mm, v(12.68, -9.5) * mm, v(12.41, -9.65) * mm, v(12.16, -9.96) * mm]});
            skFitSpline(sketch, "E107", {"points": [v(12.16, -9.96) * mm, v(11.9, -10.28) * mm, v(11.8, -10.57) * mm, v(11.86, -10.85) * mm]});
            skFitSpline(sketch, "E108", {"points": [v(11.86, -10.85) * mm, v(11.92, -11.12) * mm, v(12.14, -11.42) * mm, v(12.52, -11.73) * mm]});
            skLineSegment(sketch, "E109", {"start": v(12.52, -11.73) * mm, "end": v(14.7, -13.5) * mm});
            skLineSegment(sketch, "E110", {"start": v(14.7, -13.5) * mm, "end": v(14.31, -14) * mm});
            skLineSegment(sketch, "E111", {"start": v(14.31, -14) * mm, "end": v(12.07, -12.17) * mm});
            skFitSpline(sketch, "E112", {"points": [v(12.07, -12.17) * mm, v(11.6, -11.8) * mm, v(11.34, -11.39) * mm, v(11.29, -10.96) * mm]});
            skFitSpline(sketch, "E113", {"points": [v(11.29, -10.96) * mm, v(11.24, -10.54) * mm, v(11.4, -10.1) * mm, v(11.76, -9.64) * mm]});
            skFitSpline(sketch, "E114", {"points": [v(11.76, -9.64) * mm, v(12.13, -9.2) * mm, v(12.53, -8.94) * mm, v(12.96, -8.9) * mm]});
            skFitSpline(sketch, "E115", {"points": [v(12.96, -8.9) * mm, v(13.38, -8.87) * mm, v(13.83, -9.04) * mm, v(14.3, -9.42) * mm]});
            skLineSegment(sketch, "E116", {"start": v(14.3, -9.42) * mm, "end": v(16.54, -11.24) * mm});
            skLineSegment(sketch, "E117", {"start": v(8.26, -13.59) * mm, "end": v(7.35, -14.05) * mm});
            skLineSegment(sketch, "E118", {"start": v(7.35, -14.05) * mm, "end": v(8.95, -17.2) * mm});
            skLineSegment(sketch, "E119", {"start": v(8.95, -17.2) * mm, "end": v(9.84, -16.5) * mm});
            skLineSegment(sketch, "E120", {"start": v(9.84, -16.5) * mm, "end": v(10.1, -17) * mm});
            skLineSegment(sketch, "E121", {"start": v(10.1, -17) * mm, "end": v(9.22, -17.7) * mm});
            skLineSegment(sketch, "E122", {"start": v(9.22, -17.7) * mm, "end": v(8.66, -17.99) * mm});
            skLineSegment(sketch, "E123", {"start": v(8.66, -17.99) * mm, "end": v(6.8, -14.34) * mm});
            skLineSegment(sketch, "E124", {"start": v(6.8, -14.34) * mm, "end": v(5.88, -14.8) * mm});
            skLineSegment(sketch, "E125", {"start": v(5.88, -14.8) * mm, "end": v(5.64, -14.33) * mm});
            skLineSegment(sketch, "E126", {"start": v(5.64, -14.33) * mm, "end": v(8.02, -13.12) * mm});
            skLineSegment(sketch, "E127", {"start": v(8.02, -13.12) * mm, "end": v(8.26, -13.59) * mm});
            skFitSpline(sketch, "E128", {"points": [v(3.98, -19.15) * mm, v(4.3, -19.08) * mm, v(4.5, -18.88) * mm, v(4.6, -18.53) * mm]});
            skFitSpline(sketch, "E129", {"points": [v(4.6, -18.53) * mm, v(4.69, -18.19) * mm, v(4.67, -17.7) * mm, v(4.54, -17.08) * mm]});
            skFitSpline(sketch, "E130", {"points": [v(4.54, -17.08) * mm, v(4.41, -16.46) * mm, v(4.23, -16.01) * mm, v(4.01, -15.73) * mm]});
            skFitSpline(sketch, "E131", {"points": [v(4.01, -15.73) * mm, v(3.79, -15.46) * mm, v(3.52, -15.35) * mm, v(3.2, -15.42) * mm]});
            skFitSpline(sketch, "E132", {"points": [v(3.2, -15.42) * mm, v(2.88, -15.48) * mm, v(2.68, -15.69) * mm, v(2.59, -16.03) * mm]});
            skFitSpline(sketch, "E133", {"points": [v(2.59, -16.03) * mm, v(2.49, -16.37) * mm, v(2.5, -16.86) * mm, v(2.64, -17.48) * mm]});
            skFitSpline(sketch, "E134", {"points": [v(2.64, -17.48) * mm, v(2.77, -18.1) * mm, v(2.94, -18.55) * mm, v(3.17, -18.83) * mm]});
            skFitSpline(sketch, "E135", {"points": [v(3.17, -18.83) * mm, v(3.39, -19.1) * mm, v(3.66, -19.21) * mm, v(3.98, -19.15) * mm]});
            skFitSpline(sketch, "E136", {"points": [v(4.08, -19.63) * mm, v(3.57, -19.74) * mm, v(3.14, -19.62) * mm, v(2.79, -19.27) * mm]});
            skFitSpline(sketch, "E137", {"points": [v(2.79, -19.27) * mm, v(2.44, -18.93) * mm, v(2.18, -18.37) * mm, v(2.02, -17.6) * mm]});
            skFitSpline(sketch, "E138", {"points": [v(2.02, -17.6) * mm, v(1.86, -16.84) * mm, v(1.88, -16.23) * mm, v(2.06, -15.77) * mm]});
            skFitSpline(sketch, "E139", {"points": [v(2.06, -15.77) * mm, v(2.25, -15.32) * mm, v(2.6, -15.04) * mm, v(3.1, -14.93) * mm]});
            skFitSpline(sketch, "E140", {"points": [v(3.1, -14.93) * mm, v(3.6, -14.82) * mm, v(4.04, -14.94) * mm, v(4.4, -15.29) * mm]});
            skFitSpline(sketch, "E141", {"points": [v(4.4, -15.29) * mm, v(4.74, -15.64) * mm, v(5, -16.2) * mm, v(5.16, -16.95) * mm]});
            skFitSpline(sketch, "E142", {"points": [v(5.16, -16.95) * mm, v(5.31, -17.72) * mm, v(5.3, -18.33) * mm, v(5.12, -18.79) * mm]});
            skFitSpline(sketch, "E143", {"points": [v(5.12, -18.79) * mm, v(4.93, -19.24) * mm, v(4.59, -19.53) * mm, v(4.08, -19.63) * mm]});
            skLineSegment(sketch, "E144", {"start": v(-14.07, -14.18) * mm, "end": v(-16, -11.97) * mm});
            skLineSegment(sketch, "E145", {"start": v(-16, -11.97) * mm, "end": v(-15.6, -11.63) * mm});
            skLineSegment(sketch, "E146", {"start": v(-15.6, -11.63) * mm, "end": v(-14.09, -13.36) * mm});
            skLineSegment(sketch, "E147", {"start": v(-14.09, -13.36) * mm, "end": v(-13.05, -12.46) * mm});
            skLineSegment(sketch, "E148", {"start": v(-13.05, -12.46) * mm, "end": v(-14.5, -10.8) * mm});
            skLineSegment(sketch, "E149", {"start": v(-14.5, -10.8) * mm, "end": v(-14.1, -10.45) * mm});
            skLineSegment(sketch, "E150", {"start": v(-14.1, -10.45) * mm, "end": v(-12.65, -12.12) * mm});
            skLineSegment(sketch, "E151", {"start": v(-12.65, -12.12) * mm, "end": v(-11.39, -11.02) * mm});
            skLineSegment(sketch, "E152", {"start": v(-11.39, -11.02) * mm, "end": v(-12.93, -9.24) * mm});
            skLineSegment(sketch, "E153", {"start": v(-12.93, -9.24) * mm, "end": v(-12.54, -8.9) * mm});
            skLineSegment(sketch, "E154", {"start": v(-12.54, -8.9) * mm, "end": v(-10.58, -11.14) * mm});
            skLineSegment(sketch, "E155", {"start": v(-10.58, -11.14) * mm, "end": v(-14.07, -14.18) * mm});
            skLineSegment(sketch, "E156", {"start": v(-18.33, -7.47) * mm, "end": v(-17.78, -7.2) * mm});
            skFitSpline(sketch, "E157", {"points": [v(-17.78, -7.2) * mm, v(-17.78, -7.47) * mm, v(-17.75, -7.7) * mm, v(-17.71, -7.92) * mm]});
            skFitSpline(sketch, "E158", {"points": [v(-17.71, -7.92) * mm, v(-17.67, -8.13) * mm, v(-17.6, -8.33) * mm, v(-17.52, -8.5) * mm]});
            skFitSpline(sketch, "E159", {"points": [v(-17.52, -8.5) * mm, v(-17.37, -8.81) * mm, v(-17.2, -9.02) * mm, v(-17, -9.13) * mm]});
            skFitSpline(sketch, "E160", {"points": [v(-17, -9.13) * mm, v(-16.8, -9.24) * mm, v(-16.59, -9.24) * mm, v(-16.37, -9.13) * mm]});
            skFitSpline(sketch, "E161", {"points": [v(-16.37, -9.13) * mm, v(-16.19, -9.04) * mm, v(-16.07, -8.92) * mm, v(-16.03, -8.76) * mm]});
            skFitSpline(sketch, "E162", {"points": [v(-16.03, -8.76) * mm, v(-16, -8.6) * mm, v(-16.02, -8.36) * mm, v(-16.11, -8.02) * mm]});
            skLineSegment(sketch, "E163", {"start": v(-16.11, -8.02) * mm, "end": v(-16.2, -7.65) * mm});
            skFitSpline(sketch, "E164", {"points": [v(-16.2, -7.65) * mm, v(-16.33, -7.2) * mm, v(-16.34, -6.81) * mm, v(-16.23, -6.52) * mm]});
            skFitSpline(sketch, "E165", {"points": [v(-16.23, -6.52) * mm, v(-16.13, -6.22) * mm, v(-15.9, -5.99) * mm, v(-15.57, -5.82) * mm]});
            skFitSpline(sketch, "E166", {"points": [v(-15.57, -5.82) * mm, v(-15.17, -5.63) * mm, v(-14.8, -5.61) * mm, v(-14.46, -5.78) * mm]});
            skFitSpline(sketch, "E167", {"points": [v(-14.46, -5.78) * mm, v(-14.12, -5.95) * mm, v(-13.82, -6.3) * mm, v(-13.57, -6.82) * mm]});
            skFitSpline(sketch, "E168", {"points": [v(-13.57, -6.82) * mm, v(-13.47, -7.02) * mm, v(-13.4, -7.24) * mm, v(-13.33, -7.48) * mm]});
            skFitSpline(sketch, "E169", {"points": [v(-13.33, -7.48) * mm, v(-13.26, -7.73) * mm, v(-13.22, -7.99) * mm, v(-13.2, -8.27) * mm]});
            skLineSegment(sketch, "E170", {"start": v(-13.2, -8.27) * mm, "end": v(-13.77, -8.55) * mm});
            skFitSpline(sketch, "E171", {"points": [v(-13.77, -8.55) * mm, v(-13.75, -8.26) * mm, v(-13.77, -7.99) * mm, v(-13.8, -7.74) * mm]});
            skFitSpline(sketch, "E172", {"points": [v(-13.8, -7.74) * mm, v(-13.85, -7.49) * mm, v(-13.92, -7.25) * mm, v(-14.02, -7.04) * mm]});
            skFitSpline(sketch, "E173", {"points": [v(-14.02, -7.04) * mm, v(-14.18, -6.72) * mm, v(-14.36, -6.5) * mm, v(-14.57, -6.39) * mm]});
            skFitSpline(sketch, "E174", {"points": [v(-14.57, -6.39) * mm, v(-14.79, -6.28) * mm, v(-15, -6.28) * mm, v(-15.24, -6.4) * mm]});
            skFitSpline(sketch, "E175", {"points": [v(-15.24, -6.4) * mm, v(-15.45, -6.49) * mm, v(-15.58, -6.63) * mm, v(-15.63, -6.81) * mm]});
            skFitSpline(sketch, "E176", {"points": [v(-15.63, -6.81) * mm, v(-15.69, -7) * mm, v(-15.67, -7.24) * mm, v(-15.6, -7.56) * mm]});
            skLineSegment(sketch, "E177", {"start": v(-15.6, -7.56) * mm, "end": v(-15.5, -7.93) * mm});
            skFitSpline(sketch, "E178", {"points": [v(-15.5, -7.93) * mm, v(-15.37, -8.4) * mm, v(-15.35, -8.76) * mm, v(-15.44, -9.03) * mm]});
            skFitSpline(sketch, "E179", {"points": [v(-15.44, -9.03) * mm, v(-15.53, -9.3) * mm, v(-15.73, -9.52) * mm, v(-16.05, -9.68) * mm]});
            skFitSpline(sketch, "E180", {"points": [v(-16.05, -9.68) * mm, v(-16.42, -9.86) * mm, v(-16.77, -9.87) * mm, v(-17.1, -9.71) * mm]});
            skFitSpline(sketch, "E181", {"points": [v(-17.1, -9.71) * mm, v(-17.45, -9.55) * mm, v(-17.73, -9.25) * mm, v(-17.95, -8.8) * mm]});
            skFitSpline(sketch, "E182", {"points": [v(-17.95, -8.8) * mm, v(-18.04, -8.6) * mm, v(-18.12, -8.39) * mm, v(-18.18, -8.17) * mm]});
            skFitSpline(sketch, "E183", {"points": [v(-18.18, -8.17) * mm, v(-18.25, -7.95) * mm, v(-18.3, -7.72) * mm, v(-18.33, -7.47) * mm]});
            skLineSegment(sketch, "E184", {"start": v(-18.33, -7.47) * mm, "end": v(-18.33, -7.47) * mm});
            skLineSegment(sketch, "E185", {"start": v(-19.29, -5.14) * mm, "end": v(-19.4, -4.51) * mm});
            skLineSegment(sketch, "E186", {"start": v(-19.4, -4.51) * mm, "end": v(-16.62, -4.05) * mm});
            skFitSpline(sketch, "E187", {"points": [v(-16.62, -4.05) * mm, v(-16.13, -3.97) * mm, v(-15.8, -3.82) * mm, v(-15.6, -3.61) * mm]});
            skFitSpline(sketch, "E188", {"points": [v(-15.6, -3.61) * mm, v(-15.42, -3.4) * mm, v(-15.36, -3.1) * mm, v(-15.43, -2.7) * mm]});
            skFitSpline(sketch, "E189", {"points": [v(-15.43, -2.7) * mm, v(-15.5, -2.3) * mm, v(-15.65, -2.03) * mm, v(-15.9, -1.89) * mm]});
            skFitSpline(sketch, "E190", {"points": [v(-15.9, -1.89) * mm, v(-16.14, -1.75) * mm, v(-16.5, -1.72) * mm, v(-17, -1.8) * mm]});
            skLineSegment(sketch, "E191", {"start": v(-17, -1.8) * mm, "end": v(-19.77, -2.26) * mm});
            skLineSegment(sketch, "E192", {"start": v(-19.77, -2.26) * mm, "end": v(-19.87, -1.64) * mm});
            skLineSegment(sketch, "E193", {"start": v(-19.87, -1.64) * mm, "end": v(-17.02, -1.17) * mm});
            skFitSpline(sketch, "E194", {"points": [v(-17.02, -1.17) * mm, v(-16.42, -1.07) * mm, v(-15.95, -1.14) * mm, v(-15.6, -1.38) * mm]});
            skFitSpline(sketch, "E195", {"points": [v(-15.6, -1.38) * mm, v(-15.24, -1.63) * mm, v(-15.02, -2.04) * mm, v(-14.92, -2.61) * mm]});
            skFitSpline(sketch, "E196", {"points": [v(-14.92, -2.61) * mm, v(-14.83, -3.19) * mm, v(-14.9, -3.65) * mm, v(-15.16, -4) * mm]});
            skFitSpline(sketch, "E197", {"points": [v(-15.16, -4) * mm, v(-15.42, -4.34) * mm, v(-15.84, -4.56) * mm, v(-16.44, -4.66) * mm]});
            skLineSegment(sketch, "E198", {"start": v(-16.44, -4.66) * mm, "end": v(-19.29, -5.14) * mm});
            skLineSegment(sketch, "E199", {"start": v(-15.56, 2.63) * mm, "end": v(-15.3, 3.62) * mm});
            skLineSegment(sketch, "E200", {"start": v(-15.3, 3.62) * mm, "end": v(-18.72, 4.5) * mm});
            skLineSegment(sketch, "E201", {"start": v(-18.72, 4.5) * mm, "end": v(-18.79, 3.36) * mm});
            skLineSegment(sketch, "E202", {"start": v(-18.79, 3.36) * mm, "end": v(-19.34, 3.5) * mm});
            skLineSegment(sketch, "E203", {"start": v(-19.34, 3.5) * mm, "end": v(-19.28, 4.63) * mm});
            skLineSegment(sketch, "E204", {"start": v(-19.28, 4.63) * mm, "end": v(-19.12, 5.24) * mm});
            skLineSegment(sketch, "E205", {"start": v(-19.12, 5.24) * mm, "end": v(-15.15, 4.22) * mm});
            skLineSegment(sketch, "E206", {"start": v(-15.15, 4.22) * mm, "end": v(-14.9, 5.2) * mm});
            skLineSegment(sketch, "E207", {"start": v(-14.9, 5.2) * mm, "end": v(-14.38, 5.08) * mm});
            skLineSegment(sketch, "E208", {"start": v(-14.38, 5.08) * mm, "end": v(-15.05, 2.5) * mm});
            skLineSegment(sketch, "E209", {"start": v(-15.05, 2.5) * mm, "end": v(-15.56, 2.63) * mm});
            skFitSpline(sketch, "E210", {"points": [v(-16.89, 9.51) * mm, v(-17.05, 9.23) * mm, v(-17.03, 8.94) * mm, v(-16.84, 8.64) * mm]});
            skFitSpline(sketch, "E211", {"points": [v(-16.84, 8.64) * mm, v(-16.64, 8.35) * mm, v(-16.27, 8.04) * mm, v(-15.71, 7.73) * mm]});
            skFitSpline(sketch, "E212", {"points": [v(-15.71, 7.73) * mm, v(-15.16, 7.41) * mm, v(-14.7, 7.25) * mm, v(-14.35, 7.23) * mm]});
            skFitSpline(sketch, "E213", {"points": [v(-14.35, 7.23) * mm, v(-14, 7.21) * mm, v(-13.74, 7.35) * mm, v(-13.58, 7.63) * mm]});
            skFitSpline(sketch, "E214", {"points": [v(-13.58, 7.63) * mm, v(-13.42, 7.9) * mm, v(-13.44, 8.2) * mm, v(-13.63, 8.5) * mm]});
            skFitSpline(sketch, "E215", {"points": [v(-13.63, 8.5) * mm, v(-13.83, 8.8) * mm, v(-14.2, 9.1) * mm, v(-14.75, 9.41) * mm]});
            skFitSpline(sketch, "E216", {"points": [v(-14.75, 9.41) * mm, v(-15.3, 9.73) * mm, v(-15.76, 9.9) * mm, v(-16.11, 9.91) * mm]});
            skFitSpline(sketch, "E217", {"points": [v(-16.11, 9.91) * mm, v(-16.47, 9.93) * mm, v(-16.73, 9.8) * mm, v(-16.89, 9.51) * mm]});
            skFitSpline(sketch, "E218", {"points": [v(-17.32, 9.76) * mm, v(-17.06, 10.21) * mm, v(-16.69, 10.45) * mm, v(-16.2, 10.49) * mm]});
            skFitSpline(sketch, "E219", {"points": [v(-16.2, 10.49) * mm, v(-15.7, 10.52) * mm, v(-15.12, 10.35) * mm, v(-14.44, 9.96) * mm]});
            skFitSpline(sketch, "E220", {"points": [v(-14.44, 9.96) * mm, v(-13.76, 9.57) * mm, v(-13.31, 9.16) * mm, v(-13.1, 8.71) * mm]});
            skFitSpline(sketch, "E221", {"points": [v(-13.1, 8.71) * mm, v(-12.87, 8.28) * mm, v(-12.9, 7.83) * mm, v(-13.15, 7.38) * mm]});
            skFitSpline(sketch, "E222", {"points": [v(-13.15, 7.38) * mm, v(-13.4, 6.93) * mm, v(-13.78, 6.69) * mm, v(-14.27, 6.65) * mm]});
            skFitSpline(sketch, "E223", {"points": [v(-14.27, 6.65) * mm, v(-14.76, 6.62) * mm, v(-15.35, 6.8) * mm, v(-16.03, 7.18) * mm]});
            skFitSpline(sketch, "E224", {"points": [v(-16.03, 7.18) * mm, v(-16.7, 7.57) * mm, v(-17.15, 7.98) * mm, v(-17.37, 8.42) * mm]});
            skFitSpline(sketch, "E225", {"points": [v(-17.37, 8.42) * mm, v(-17.6, 8.86) * mm, v(-17.58, 9.3) * mm, v(-17.32, 9.76) * mm]});
            skLineSegment(sketch, "E226", {"start": v(-2.73, 15.42) * mm, "end": v(-0.56, 15.7) * mm});
            skLineSegment(sketch, "E227", {"start": v(-0.56, 15.7) * mm, "end": v(-0.5, 15.17) * mm});
            skLineSegment(sketch, "E228", {"start": v(-0.5, 15.17) * mm, "end": v(-3.42, 14.8) * mm});
            skLineSegment(sketch, "E229", {"start": v(-3.42, 14.8) * mm, "end": v(-3.48, 15.33) * mm});
            skFitSpline(sketch, "E230", {"points": [v(-3.48, 15.33) * mm, v(-3.28, 15.6) * mm, v(-3, 15.97) * mm, v(-2.64, 16.43) * mm]});
            skFitSpline(sketch, "E231", {"points": [v(-2.64, 16.43) * mm, v(-2.28, 16.9) * mm, v(-2.06, 17.2) * mm, v(-1.97, 17.32) * mm]});
            skFitSpline(sketch, "E232", {"points": [v(-1.97, 17.32) * mm, v(-1.8, 17.57) * mm, v(-1.68, 17.78) * mm, v(-1.62, 17.94) * mm]});
            skFitSpline(sketch, "E233", {"points": [v(-1.62, 17.94) * mm, v(-1.56, 18.1) * mm, v(-1.54, 18.26) * mm, v(-1.56, 18.41) * mm]});
            skFitSpline(sketch, "E234", {"points": [v(-1.56, 18.41) * mm, v(-1.59, 18.66) * mm, v(-1.7, 18.85) * mm, v(-1.9, 18.98) * mm]});
            skFitSpline(sketch, "E235", {"points": [v(-1.9, 18.98) * mm, v(-2.08, 19.11) * mm, v(-2.31, 19.16) * mm, v(-2.59, 19.13) * mm]});
            skFitSpline(sketch, "E236", {"points": [v(-2.59, 19.13) * mm, v(-2.78, 19.1) * mm, v(-2.98, 19.04) * mm, v(-3.2, 18.95) * mm]});
            skFitSpline(sketch, "E237", {"points": [v(-3.2, 18.95) * mm, v(-3.4, 18.86) * mm, v(-3.62, 18.73) * mm, v(-3.85, 18.56) * mm]});
            skLineSegment(sketch, "E238", {"start": v(-3.85, 18.56) * mm, "end": v(-3.92, 19.19) * mm});
            skFitSpline(sketch, "E239", {"points": [v(-3.92, 19.19) * mm, v(-3.69, 19.32) * mm, v(-3.46, 19.42) * mm, v(-3.25, 19.5) * mm]});
            skFitSpline(sketch, "E240", {"points": [v(-3.25, 19.5) * mm, v(-3.04, 19.58) * mm, v(-2.84, 19.63) * mm, v(-2.66, 19.65) * mm]});
            skFitSpline(sketch, "E241", {"points": [v(-2.66, 19.65) * mm, v(-2.19, 19.7) * mm, v(-1.8, 19.64) * mm, v(-1.48, 19.43) * mm]});
            skFitSpline(sketch, "E242", {"points": [v(-1.48, 19.43) * mm, v(-1.17, 19.23) * mm, v(-0.99, 18.93) * mm, v(-0.94, 18.53) * mm]});
            skFitSpline(sketch, "E243", {"points": [v(-0.94, 18.53) * mm, v(-0.92, 18.34) * mm, v(-0.93, 18.16) * mm, v(-0.98, 17.98) * mm]});
            skFitSpline(sketch, "E244", {"points": [v(-0.98, 17.98) * mm, v(-1.03, 17.8) * mm, v(-1.13, 17.59) * mm, v(-1.3, 17.34) * mm]});
            skFitSpline(sketch, "E245", {"points": [v(-1.3, 17.34) * mm, v(-1.34, 17.27) * mm, v(-1.48, 17.08) * mm, v(-1.72, 16.76) * mm]});
            skFitSpline(sketch, "E246", {"points": [v(-1.72, 16.76) * mm, v(-1.96, 16.44) * mm, v(-2.3, 16) * mm, v(-2.73, 15.42) * mm]});
            skFitSpline(sketch, "E247", {"points": [v(2.75, 19.14) * mm, v(2.43, 19.18) * mm, v(2.17, 19.06) * mm, v(1.96, 18.77) * mm]});
            skFitSpline(sketch, "E248", {"points": [v(1.96, 18.77) * mm, v(1.76, 18.48) * mm, v(1.61, 18.02) * mm, v(1.52, 17.39) * mm]});
            skFitSpline(sketch, "E249", {"points": [v(1.52, 17.39) * mm, v(1.43, 16.76) * mm, v(1.44, 16.27) * mm, v(1.56, 15.94) * mm]});
            skFitSpline(sketch, "E250", {"points": [v(1.56, 15.94) * mm, v(1.68, 15.6) * mm, v(1.9, 15.41) * mm, v(2.21, 15.36) * mm]});
            skFitSpline(sketch, "E251", {"points": [v(2.21, 15.36) * mm, v(2.54, 15.32) * mm, v(2.8, 15.44) * mm, v(3, 15.73) * mm]});
            skFitSpline(sketch, "E252", {"points": [v(3, 15.73) * mm, v(3.2, 16.02) * mm, v(3.36, 16.48) * mm, v(3.45, 17.11) * mm]});
            skFitSpline(sketch, "E253", {"points": [v(3.45, 17.11) * mm, v(3.53, 17.74) * mm, v(3.52, 18.23) * mm, v(3.4, 18.56) * mm]});
            skFitSpline(sketch, "E254", {"points": [v(3.4, 18.56) * mm, v(3.29, 18.9) * mm, v(3.07, 19.1) * mm, v(2.75, 19.14) * mm]});
            skFitSpline(sketch, "E255", {"points": [v(2.82, 19.63) * mm, v(3.33, 19.56) * mm, v(3.7, 19.3) * mm, v(3.9, 18.85) * mm]});
            skFitSpline(sketch, "E256", {"points": [v(3.9, 18.85) * mm, v(4.12, 18.4) * mm, v(4.18, 17.8) * mm, v(4.07, 17.02) * mm]});
            skFitSpline(sketch, "E257", {"points": [v(4.07, 17.02) * mm, v(3.96, 16.25) * mm, v(3.74, 15.68) * mm, v(3.4, 15.31) * mm]});
            skFitSpline(sketch, "E258", {"points": [v(3.4, 15.31) * mm, v(3.08, 14.95) * mm, v(2.66, 14.8) * mm, v(2.14, 14.87) * mm]});
            skFitSpline(sketch, "E259", {"points": [v(2.14, 14.87) * mm, v(1.63, 14.95) * mm, v(1.27, 15.2) * mm, v(1.05, 15.65) * mm]});
            skFitSpline(sketch, "E260", {"points": [v(1.05, 15.65) * mm, v(0.84, 16.1) * mm, v(0.79, 16.7) * mm, v(0.9, 17.47) * mm]});
            skFitSpline(sketch, "E261", {"points": [v(0.9, 17.47) * mm, v(1, 18.25) * mm, v(1.23, 18.82) * mm, v(1.55, 19.19) * mm]});
            skFitSpline(sketch, "E262", {"points": [v(1.55, 19.19) * mm, v(1.88, 19.55) * mm, v(2.3, 19.7) * mm, v(2.82, 19.63) * mm]});
            skLineSegment(sketch, "E263", {"start": v(5.12, 14.84) * mm, "end": v(6.06, 14.44) * mm});
            skLineSegment(sketch, "E264", {"start": v(6.06, 14.44) * mm, "end": v(7.46, 17.68) * mm});
            skLineSegment(sketch, "E265", {"start": v(7.46, 17.68) * mm, "end": v(6.35, 17.92) * mm});
            skLineSegment(sketch, "E266", {"start": v(6.35, 17.92) * mm, "end": v(6.57, 18.44) * mm});
            skLineSegment(sketch, "E267", {"start": v(6.57, 18.44) * mm, "end": v(7.68, 18.2) * mm});
            skLineSegment(sketch, "E268", {"start": v(7.68, 18.2) * mm, "end": v(8.25, 17.96) * mm});
            skLineSegment(sketch, "E269", {"start": v(8.25, 17.96) * mm, "end": v(6.63, 14.2) * mm});
            skLineSegment(sketch, "E270", {"start": v(6.63, 14.2) * mm, "end": v(7.56, 13.79) * mm});
            skLineSegment(sketch, "E271", {"start": v(7.56, 13.79) * mm, "end": v(7.36, 13.3) * mm});
            skLineSegment(sketch, "E272", {"start": v(7.36, 13.3) * mm, "end": v(4.9, 14.36) * mm});
            skLineSegment(sketch, "E273", {"start": v(4.9, 14.36) * mm, "end": v(5.12, 14.84) * mm});
            skFitSpline(sketch, "E274", {"points": [v(11.15, 13.75) * mm, v(10.93, 13.93) * mm, v(10.7, 14) * mm, v(10.45, 13.94) * mm]});
            skFitSpline(sketch, "E275", {"points": [v(10.45, 13.94) * mm, v(10.2, 13.9) * mm, v(9.97, 13.74) * mm, v(9.77, 13.48) * mm]});
            skFitSpline(sketch, "E276", {"points": [v(9.77, 13.48) * mm, v(9.56, 13.22) * mm, v(9.46, 12.96) * mm, v(9.46, 12.7) * mm]});
            skFitSpline(sketch, "E277", {"points": [v(9.46, 12.7) * mm, v(9.47, 12.46) * mm, v(9.59, 12.24) * mm, v(9.8, 12.07) * mm]});
            skFitSpline(sketch, "E278", {"points": [v(9.8, 12.07) * mm, v(10.03, 11.89) * mm, v(10.26, 11.83) * mm, v(10.5, 11.87) * mm]});
            skFitSpline(sketch, "E279", {"points": [v(10.5, 11.87) * mm, v(10.76, 11.92) * mm, v(10.99, 12.08) * mm, v(11.2, 12.34) * mm]});
            skFitSpline(sketch, "E280", {"points": [v(11.2, 12.34) * mm, v(11.4, 12.6) * mm, v(11.5, 12.86) * mm, v(11.5, 13.11) * mm]});
            skFitSpline(sketch, "E281", {"points": [v(11.5, 13.11) * mm, v(11.49, 13.36) * mm, v(11.37, 13.58) * mm, v(11.15, 13.75) * mm]});
            skLineSegment(sketch, "E282", {"start": v(13.35, 14.51) * mm, "end": v(13, 14.06) * mm});
            skFitSpline(sketch, "E283", {"points": [v(13, 14.06) * mm, v(12.92, 14.22) * mm, v(12.83, 14.36) * mm, v(12.73, 14.5) * mm]});
            skFitSpline(sketch, "E284", {"points": [v(12.73, 14.5) * mm, v(12.63, 14.63) * mm, v(12.52, 14.74) * mm, v(12.4, 14.84) * mm]});
            skFitSpline(sketch, "E285", {"points": [v(12.4, 14.84) * mm, v(12.07, 15.1) * mm, v(11.74, 15.18) * mm, v(11.4, 15.1) * mm]});
            skFitSpline(sketch, "E286", {"points": [v(11.4, 15.1) * mm, v(11.05, 15.02) * mm, v(10.69, 14.77) * mm, v(10.31, 14.35) * mm]});
            skFitSpline(sketch, "E287", {"points": [v(10.31, 14.35) * mm, v(10.52, 14.41) * mm, v(10.72, 14.42) * mm, v(10.93, 14.38) * mm]});
            skFitSpline(sketch, "E288", {"points": [v(10.93, 14.38) * mm, v(11.13, 14.34) * mm, v(11.32, 14.25) * mm, v(11.5, 14.12) * mm]});
            skFitSpline(sketch, "E289", {"points": [v(11.5, 14.12) * mm, v(11.86, 13.83) * mm, v(12.05, 13.49) * mm, v(12.09, 13.1) * mm]});
            skFitSpline(sketch, "E290", {"points": [v(12.09, 13.1) * mm, v(12.12, 12.7) * mm, v(12, 12.33) * mm, v(11.69, 11.95) * mm]});
            skFitSpline(sketch, "E291", {"points": [v(11.69, 11.95) * mm, v(11.4, 11.57) * mm, v(11.04, 11.36) * mm, v(10.64, 11.31) * mm]});
            skFitSpline(sketch, "E292", {"points": [v(10.64, 11.31) * mm, v(10.25, 11.27) * mm, v(9.86, 11.39) * mm, v(9.5, 11.68) * mm]});
            skFitSpline(sketch, "E293", {"points": [v(9.5, 11.68) * mm, v(9.08, 12.01) * mm, v(8.89, 12.43) * mm, v(8.92, 12.92) * mm]});
            skFitSpline(sketch, "E294", {"points": [v(8.92, 12.92) * mm, v(8.96, 13.42) * mm, v(9.22, 13.98) * mm, v(9.7, 14.58) * mm]});
            skFitSpline(sketch, "E295", {"points": [v(9.7, 14.58) * mm, v(10.16, 15.16) * mm, v(10.66, 15.5) * mm, v(11.2, 15.63) * mm]});
            skFitSpline(sketch, "E296", {"points": [v(11.2, 15.63) * mm, v(11.74, 15.75) * mm, v(12.25, 15.63) * mm, v(12.7, 15.27) * mm]});
            skFitSpline(sketch, "E297", {"points": [v(12.7, 15.27) * mm, v(12.83, 15.17) * mm, v(12.94, 15.06) * mm, v(13.04, 14.93) * mm]});
            skFitSpline(sketch, "E298", {"points": [v(13.04, 14.93) * mm, v(13.15, 14.8) * mm, v(13.25, 14.67) * mm, v(13.35, 14.51) * mm]});
            skSolve(sketch);
        }
        {
            var Q0;
            {var subQ5=sQuery(id+"F26.wireOp",EDGE,"E263");Q0=makeQuery(id+"F26.imprint","IMPRINT",FACE,{"disambiguationData":[TD([[makeQuery(id+"F26.imprint","IMPRINT",EDGE,{"derivedFrom":subQ5}),-1.0]])]});}
            var Q1;
            {var subQ0=sQuery(id+"F26.wireOp",EDGE,"E272");Q1=makeQuery(id+"F26.imprint","IMPRINT",FACE,{"disambiguationData":[TD([[makeQuery(id+"F26.imprint","IMPRINT",EDGE,{"derivedFrom":subQ0}),-1.0]])]});}
            var Q2;
            Q2=makeQuery(id+"F26.imprint","IMPRINT",FACE,{"disambiguationData":[TD([[makeQuery(id+"F26.imprint","IMPRINT",EDGE,{"derivedFrom":sQuery(id+"F26.wireOp",EDGE,"E274")}),-1.0]])]});
            var Q3;
            {var subQ0=sQuery(id+"F26.wireOp",EDGE,"E293");var subQ1=sQuery(id+"F26.wireOp",EDGE,"E60");var subQ2=makeQuery(id+"F26.imprint","INTERSECT",VERTEX,{"derivedFrom":[subQ1,subQ0]});Q3=makeQuery(id+"F26.imprint","IMPRINT",FACE,{"disambiguationData":[TD([[makeQuery(id+"F26.imprint","IMPRINT",EDGE,{"disambiguationData":[TD([[subQ2,-1.0]])],"derivedFrom":subQ1}),1.0]])]});}
            var Q4;
            Q4=makeQuery(id+"F26.imprint","IMPRINT",FACE,{"disambiguationData":[TD([[makeQuery(id+"F26.imprint","IMPRINT",EDGE,{"derivedFrom":sQuery(id+"F26.wireOp",EDGE,"E247")}),-1.0]])]});
            var Q5;
            {var subQ0=sQuery(id+"F26.wireOp",EDGE,"E259");var subQ1=sQuery(id+"F26.wireOp",EDGE,"E60");var subQ2=makeQuery(id+"F26.imprint","INTERSECT",VERTEX,{"derivedFrom":[subQ1,subQ0]});Q5=makeQuery(id+"F26.imprint","IMPRINT",FACE,{"disambiguationData":[TD([[makeQuery(id+"F26.imprint","IMPRINT",EDGE,{"disambiguationData":[TD([[subQ2,-1.0]])],"derivedFrom":subQ1}),1.0]])]});}
            var Q6;
            {var subQ6=sQuery(id+"F26.wireOp",EDGE,"E226");Q6=makeQuery(id+"F26.imprint","IMPRINT",FACE,{"disambiguationData":[TD([[makeQuery(id+"F26.imprint","IMPRINT",EDGE,{"derivedFrom":subQ6}),-1.0]])]});}
            var Q7;
            {var subQ0=sQuery(id+"F26.wireOp",EDGE,"E228");Q7=makeQuery(id+"F26.imprint","IMPRINT",FACE,{"disambiguationData":[TD([[makeQuery(id+"F26.imprint","IMPRINT",EDGE,{"derivedFrom":subQ0}),-1.0]])]});}
            var Q8;
            {var subQ5=sQuery(id+"F26.wireOp",EDGE,"E62");Q8=makeQuery(id+"F26.imprint","IMPRINT",FACE,{"disambiguationData":[TD([[makeQuery(id+"F26.imprint","IMPRINT",EDGE,{"derivedFrom":subQ5}),-1.0]])]});}
            var Q9;
            {var subQ0=sQuery(id+"F26.wireOp",EDGE,"E72");Q9=makeQuery(id+"F26.imprint","IMPRINT",FACE,{"disambiguationData":[TD([[makeQuery(id+"F26.imprint","IMPRINT",EDGE,{"derivedFrom":subQ0}),-1.0]])]});}
            var Q10;
            Q10=makeQuery(id+"F26.imprint","IMPRINT",FACE,{"disambiguationData":[TD([[makeQuery(id+"F26.imprint","IMPRINT",EDGE,{"derivedFrom":sQuery(id+"F26.wireOp",EDGE,"E74")}),-1.0]])]});
            var Q11;
            {var subQ1=sQuery(id+"F26.wireOp",EDGE,"E86");var subQ6=sQuery(id+"F26.wireOp",EDGE,"E54");var subQ7=makeQuery(id+"F26.imprint","INTERSECT",VERTEX,{"derivedFrom":[subQ6,subQ1]});Q11=makeQuery(id+"F26.imprint","IMPRINT",FACE,{"disambiguationData":[TD([[makeQuery(id+"F26.imprint","IMPRINT",EDGE,{"disambiguationData":[TD([[subQ7,-1.0]])],"derivedFrom":subQ6}),1.0]])]});}
            var Q12;
            Q12=makeQuery(id+"F26.imprint","IMPRINT",FACE,{"disambiguationData":[TD([[makeQuery(id+"F26.imprint","IMPRINT",EDGE,{"derivedFrom":sQuery(id+"F26.wireOp",EDGE,"E103")}),-1.0]])]});
            var Q13;
            {var subQ0=sQuery(id+"F26.wireOp",EDGE,"E114");var subQ1=sQuery(id+"F26.wireOp",EDGE,"E54");var subQ2=makeQuery(id+"F26.imprint","INTERSECT",VERTEX,{"derivedFrom":[subQ1,subQ0]});Q13=makeQuery(id+"F26.imprint","IMPRINT",FACE,{"disambiguationData":[TD([[makeQuery(id+"F26.imprint","IMPRINT",EDGE,{"disambiguationData":[TD([[subQ2,-1.0]])],"derivedFrom":subQ1}),1.0]])]});}
            var Q14;
            {var subQ5=sQuery(id+"F26.wireOp",EDGE,"E117");Q14=makeQuery(id+"F26.imprint","IMPRINT",FACE,{"disambiguationData":[TD([[makeQuery(id+"F26.imprint","IMPRINT",EDGE,{"derivedFrom":subQ5}),-1.0]])]});}
            var Q15;
            {var subQ0=sQuery(id+"F26.wireOp",EDGE,"E126");Q15=makeQuery(id+"F26.imprint","IMPRINT",FACE,{"disambiguationData":[TD([[makeQuery(id+"F26.imprint","IMPRINT",EDGE,{"derivedFrom":subQ0}),-1.0]])]});}
            var Q16;
            Q16=makeQuery(id+"F26.imprint","IMPRINT",FACE,{"disambiguationData":[TD([[makeQuery(id+"F26.imprint","IMPRINT",EDGE,{"derivedFrom":sQuery(id+"F26.wireOp",EDGE,"E128")}),-1.0]])]});
            var Q17;
            {var subQ0=sQuery(id+"F26.wireOp",EDGE,"E140");var subQ1=sQuery(id+"F26.wireOp",EDGE,"E55");var subQ2=makeQuery(id+"F26.imprint","INTERSECT",VERTEX,{"derivedFrom":[subQ1,subQ0]});Q17=makeQuery(id+"F26.imprint","IMPRINT",FACE,{"disambiguationData":[TD([[makeQuery(id+"F26.imprint","IMPRINT",EDGE,{"disambiguationData":[TD([[subQ2,-1.0]])],"derivedFrom":subQ1}),1.0]])]});}
            var Q18;
            {var subQ5=sQuery(id+"F26.wireOp",EDGE,"E144");Q18=makeQuery(id+"F26.imprint","IMPRINT",FACE,{"disambiguationData":[TD([[makeQuery(id+"F26.imprint","IMPRINT",EDGE,{"derivedFrom":subQ5}),-1.0]])]});}
            var Q19;
            {var subQ0=sQuery(id+"F26.wireOp",EDGE,"E154");Q19=makeQuery(id+"F26.imprint","IMPRINT",FACE,{"disambiguationData":[TD([[makeQuery(id+"F26.imprint","IMPRINT",EDGE,{"derivedFrom":subQ0}),-1.0]])]});}
            var Q20;
            Q20=makeQuery(id+"F26.imprint","IMPRINT",FACE,{"disambiguationData":[TD([[makeQuery(id+"F26.imprint","IMPRINT",EDGE,{"derivedFrom":sQuery(id+"F26.wireOp",EDGE,"E156")}),-1.0]])]});
            var Q21;
            {var subQ1=sQuery(id+"F26.wireOp",EDGE,"E168");var subQ7=sQuery(id+"F26.wireOp",EDGE,"E57");var subQ10=makeQuery(id+"F26.imprint","INTERSECT",VERTEX,{"derivedFrom":[subQ7,subQ1]});Q21=makeQuery(id+"F26.imprint","IMPRINT",FACE,{"disambiguationData":[TD([[makeQuery(id+"F26.imprint","IMPRINT",EDGE,{"disambiguationData":[TD([[subQ10,-1.0]])],"derivedFrom":subQ7}),1.0]])]});}
            var Q22;
            Q22=makeQuery(id+"F26.imprint","IMPRINT",FACE,{"disambiguationData":[TD([[makeQuery(id+"F26.imprint","IMPRINT",EDGE,{"derivedFrom":sQuery(id+"F26.wireOp",EDGE,"E185")}),-1.0]])]});
            var Q23;
            {var subQ0=sQuery(id+"F26.wireOp",EDGE,"E196");var subQ1=sQuery(id+"F26.wireOp",EDGE,"E57");var subQ2=makeQuery(id+"F26.imprint","INTERSECT",VERTEX,{"derivedFrom":[subQ1,subQ0]});Q23=makeQuery(id+"F26.imprint","IMPRINT",FACE,{"disambiguationData":[TD([[makeQuery(id+"F26.imprint","IMPRINT",EDGE,{"disambiguationData":[TD([[subQ2,-1.0]])],"derivedFrom":subQ1}),1.0]])]});}
            var Q24;
            {var subQ5=sQuery(id+"F26.wireOp",EDGE,"E199");Q24=makeQuery(id+"F26.imprint","IMPRINT",FACE,{"disambiguationData":[TD([[makeQuery(id+"F26.imprint","IMPRINT",EDGE,{"derivedFrom":subQ5}),-1.0]])]});}
            var Q25;
            {var subQ0=sQuery(id+"F26.wireOp",EDGE,"E208");Q25=makeQuery(id+"F26.imprint","IMPRINT",FACE,{"disambiguationData":[TD([[makeQuery(id+"F26.imprint","IMPRINT",EDGE,{"derivedFrom":subQ0}),-1.0]])]});}
            var Q26;
            Q26=makeQuery(id+"F26.imprint","IMPRINT",FACE,{"disambiguationData":[TD([[makeQuery(id+"F26.imprint","IMPRINT",EDGE,{"derivedFrom":sQuery(id+"F26.wireOp",EDGE,"E210")}),-1.0]])]});
            var Q27;
            {var subQ0=sQuery(id+"F26.wireOp",EDGE,"E222");var subQ1=sQuery(id+"F26.wireOp",EDGE,"E58");var subQ2=makeQuery(id+"F26.imprint","INTERSECT",VERTEX,{"derivedFrom":[subQ1,subQ0]});Q27=makeQuery(id+"F26.imprint","IMPRINT",FACE,{"disambiguationData":[TD([[makeQuery(id+"F26.imprint","IMPRINT",EDGE,{"disambiguationData":[TD([[subQ2,-1.0]])],"derivedFrom":subQ1}),1.0]])]});}
            extrude(context, id + "F27", {"entities" : qUnion([Q0, Q1, Q2, Q3, Q4, Q5, Q6, Q7, Q8, Q9, Q10, Q11, Q12, Q13, Q14, Q15, Q16, Q17, Q18, Q19, Q20, Q21, Q22, Q23, Q24, Q25, Q26, Q27]), "operationType" : NewBodyOperationType.ADD, "depth" : 1 * mm});
        }
    });
